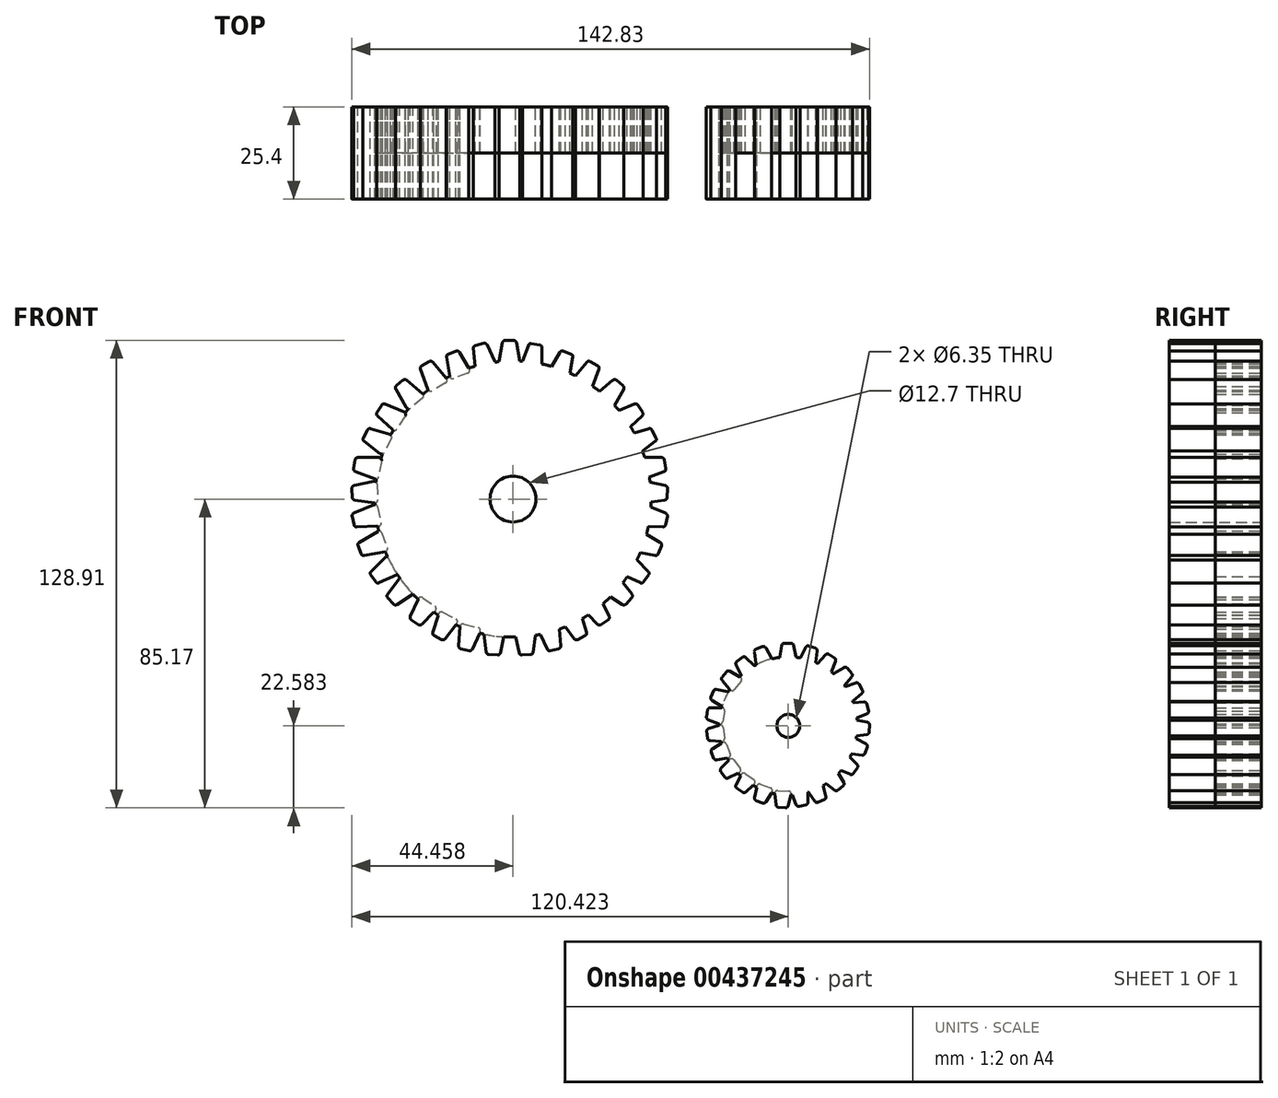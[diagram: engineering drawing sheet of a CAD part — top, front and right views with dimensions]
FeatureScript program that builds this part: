
annotation { "Feature Type Name" : "Feature", "Feature Type Description" : "" }
export const myFeature = defineFeature(function(context is Context, id is Id, definition is map)
    precondition{}
    {
        {
            var Q0;
            Q0=qCreatedBy(makeId("Front.planeOp"),FACE);
            var sketch = newSketch(context, id + "F0", { "sketchPlane" : qUnion([Q0])});
            skCircle(sketch, "E0", {"center": v(-38, 35.4) * mm, "radius": 38.1 * mm});
            skCircle(sketch, "E1", {"center": v(-38, 35.4) * mm, "radius": 6.35 * mm});
            skCircle(sketch, "E2", {"center": v(37.96, -27.19) * mm, "radius": 19.05 * mm});
            skCircle(sketch, "E3", {"center": v(37.96, -27.19) * mm, "radius": 3.18 * mm});
            skLineSegment(sketch, "E4", {"start": v(-32.93, 78.31) * mm, "end": v(-30.61, 77.9) * mm});
            skLineSegment(sketch, "E5", {"start": v(-33.78, 77.82) * mm, "end": v(-35.6, 72.8) * mm});
            skLineSegment(sketch, "E6", {"start": v(-29.98, 77.15) * mm, "end": v(-29.98, 71.81) * mm});
            skLineSegment(sketch, "E7", {"start": v(-35.02, 71.8) * mm, "end": v(-30.88, 71.06) * mm});
            skArc(sketch, "E8.filletArc", {"start": v(-32.93, 78.31) * mm, "mid": v(-33.45, 78.22) * mm, "end": v(-33.78, 77.82) * mm});
            skArc(sketch, "E9.filletArc", {"start": v(-29.98, 77.15) * mm, "mid": v(-30.16, 77.64) * mm, "end": v(-30.61, 77.9) * mm});
            skArc(sketch, "E10.filletArc", {"start": v(-30.88, 71.06) * mm, "mid": v(-30.25, 71.23) * mm, "end": v(-29.98, 71.81) * mm});
            skArc(sketch, "E11.filletArc", {"start": v(-35.6, 72.8) * mm, "mid": v(-35.55, 72.16) * mm, "end": v(-35.02, 71.8) * mm});
            skLineSegment(sketch, "E12", {"start": v(-24.2, 76.17) * mm, "end": v(-21.98, 75.37) * mm});
            skLineSegment(sketch, "E13", {"start": v(-25.11, 75.84) * mm, "end": v(-27.78, 71.21) * mm});
            skLineSegment(sketch, "E14", {"start": v(-21.49, 74.52) * mm, "end": v(-22.41, 69.26) * mm});
            skLineSegment(sketch, "E15", {"start": v(-27.38, 70.12) * mm, "end": v(-23.43, 68.68) * mm});
            skArc(sketch, "E16.filletArc", {"start": v(-24.2, 76.17) * mm, "mid": v(-24.71, 76.17) * mm, "end": v(-25.11, 75.84) * mm});
            skArc(sketch, "E17.filletArc", {"start": v(-21.49, 74.52) * mm, "mid": v(-21.58, 75.03) * mm, "end": v(-21.98, 75.37) * mm});
            skArc(sketch, "E18.filletArc", {"start": v(-23.43, 68.68) * mm, "mid": v(-22.78, 68.73) * mm, "end": v(-22.41, 69.26) * mm});
            skArc(sketch, "E19.filletArc", {"start": v(-27.78, 71.21) * mm, "mid": v(-27.84, 70.57) * mm, "end": v(-27.38, 70.12) * mm});
            skLineSegment(sketch, "E20", {"start": v(-16.67, 73.32) * mm, "end": v(-14.63, 72.15) * mm});
            skLineSegment(sketch, "E21", {"start": v(-17.63, 73.15) * mm, "end": v(-21.46, 68.6) * mm});
            skLineSegment(sketch, "E22", {"start": v(-14.3, 71.23) * mm, "end": v(-16.33, 65.64) * mm});
            skLineSegment(sketch, "E23", {"start": v(-21.25, 67.45) * mm, "end": v(-17.42, 65.24) * mm});
            skArc(sketch, "E24.filletArc", {"start": v(-16.67, 73.32) * mm, "mid": v(-17.18, 73.42) * mm, "end": v(-17.63, 73.15) * mm});
            skArc(sketch, "E25.filletArc", {"start": v(-14.3, 71.23) * mm, "mid": v(-14.3, 71.75) * mm, "end": v(-14.63, 72.15) * mm});
            skArc(sketch, "E26.filletArc", {"start": v(-17.42, 65.24) * mm, "mid": v(-16.78, 65.18) * mm, "end": v(-16.33, 65.64) * mm});
            skArc(sketch, "E27.filletArc", {"start": v(-21.46, 68.6) * mm, "mid": v(-21.62, 67.98) * mm, "end": v(-21.25, 67.45) * mm});
            skLineSegment(sketch, "E28", {"start": v(-9.46, 68.17) * mm, "end": v(-7.65, 66.66) * mm});
            skLineSegment(sketch, "E29", {"start": v(-10.44, 68.17) * mm, "end": v(-14.87, 64.45) * mm});
            skLineSegment(sketch, "E30", {"start": v(-7.48, 65.7) * mm, "end": v(-10.38, 60.68) * mm});
            skLineSegment(sketch, "E31", {"start": v(-14.87, 63.28) * mm, "end": v(-11.53, 60.48) * mm});
            skArc(sketch, "E32.filletArc", {"start": v(-9.46, 68.17) * mm, "mid": v(-9.95, 68.35) * mm, "end": v(-10.44, 68.17) * mm});
            skArc(sketch, "E33.filletArc", {"start": v(-7.48, 65.7) * mm, "mid": v(-7.4, 66.2) * mm, "end": v(-7.65, 66.66) * mm});
            skArc(sketch, "E34.filletArc", {"start": v(-11.53, 60.48) * mm, "mid": v(-10.9, 60.3) * mm, "end": v(-10.38, 60.68) * mm});
            skArc(sketch, "E35.filletArc", {"start": v(-14.87, 64.45) * mm, "mid": v(-15.15, 63.87) * mm, "end": v(-14.87, 63.28) * mm});
            skLineSegment(sketch, "E36", {"start": v(-3.53, 61.31) * mm, "end": v(-2.26, 59.32) * mm});
            skLineSegment(sketch, "E37", {"start": v(-4.47, 61.6) * mm, "end": v(-9.74, 59.41) * mm});
            skLineSegment(sketch, "E38", {"start": v(-2.4, 58.35) * mm, "end": v(-6.6, 54.49) * mm});
            skLineSegment(sketch, "E39", {"start": v(-10.09, 58.3) * mm, "end": v(-7.75, 54.64) * mm});
            skArc(sketch, "E40.filletArc", {"start": v(-3.53, 61.31) * mm, "mid": v(-3.95, 61.63) * mm, "end": v(-4.47, 61.6) * mm});
            skArc(sketch, "E41.filletArc", {"start": v(-2.4, 58.35) * mm, "mid": v(-2.15, 58.81) * mm, "end": v(-2.26, 59.32) * mm});
            skArc(sketch, "E42.filletArc", {"start": v(-7.75, 54.64) * mm, "mid": v(-7.2, 54.3) * mm, "end": v(-6.6, 54.49) * mm});
            skArc(sketch, "E43.filletArc", {"start": v(-9.74, 59.41) * mm, "mid": v(-10.17, 58.94) * mm, "end": v(-10.09, 58.3) * mm});
            skLineSegment(sketch, "E44", {"start": v(0.36, 54.44) * mm, "end": v(1.48, 52.26) * mm});
            skLineSegment(sketch, "E45", {"start": v(-0.54, 54.82) * mm, "end": v(-5.83, 53.19) * mm});
            skLineSegment(sketch, "E46", {"start": v(1.26, 51.3) * mm, "end": v(-3.15, 47.96) * mm});
            skLineSegment(sketch, "E47", {"start": v(-6.29, 52.11) * mm, "end": v(-4.3, 48.22) * mm});
            skArc(sketch, "E48.filletArc", {"start": v(0.36, 54.44) * mm, "mid": v(-0.02, 54.8) * mm, "end": v(-0.54, 54.82) * mm});
            skArc(sketch, "E49.filletArc", {"start": v(1.26, 51.3) * mm, "mid": v(1.54, 51.75) * mm, "end": v(1.48, 52.26) * mm});
            skArc(sketch, "E50.filletArc", {"start": v(-4.3, 48.22) * mm, "mid": v(-3.78, 47.83) * mm, "end": v(-3.15, 47.96) * mm});
            skArc(sketch, "E51.filletArc", {"start": v(-5.83, 53.19) * mm, "mid": v(-6.31, 52.76) * mm, "end": v(-6.29, 52.11) * mm});
            skLineSegment(sketch, "E52", {"start": v(3.74, 46.22) * mm, "end": v(4.16, 43.8) * mm});
            skLineSegment(sketch, "E53", {"start": v(2.99, 46.85) * mm, "end": v(-2.8, 46.85) * mm});
            skLineSegment(sketch, "E54", {"start": v(3.67, 42.95) * mm, "end": v(-1.76, 40.97) * mm});
            skLineSegment(sketch, "E55", {"start": v(-3.54, 45.95) * mm, "end": v(-2.77, 41.56) * mm});
            skArc(sketch, "E56.filletArc", {"start": v(3.74, 46.22) * mm, "mid": v(3.48, 46.67) * mm, "end": v(2.99, 46.85) * mm});
            skArc(sketch, "E57.filletArc", {"start": v(3.67, 42.95) * mm, "mid": v(4.07, 43.29) * mm, "end": v(4.16, 43.8) * mm});
            skArc(sketch, "E58.filletArc", {"start": v(-2.77, 41.56) * mm, "mid": v(-2.4, 41.03) * mm, "end": v(-1.76, 40.97) * mm});
            skArc(sketch, "E59.filletArc", {"start": v(-2.8, 46.85) * mm, "mid": v(-3.38, 46.58) * mm, "end": v(-3.54, 45.95) * mm});
            skLineSegment(sketch, "E60", {"start": v(4.62, 38.32) * mm, "end": v(4.52, 35.84) * mm});
            skLineSegment(sketch, "E61", {"start": v(4.03, 39.1) * mm, "end": v(-1.4, 40.3) * mm});
            skLineSegment(sketch, "E62", {"start": v(3.86, 35.11) * mm, "end": v(-1.66, 34.38) * mm});
            skLineSegment(sketch, "E63", {"start": v(-2.33, 39.58) * mm, "end": v(-2.52, 35.17) * mm});
            skArc(sketch, "E64.filletArc", {"start": v(4.62, 38.32) * mm, "mid": v(4.47, 38.82) * mm, "end": v(4.03, 39.1) * mm});
            skArc(sketch, "E65.filletArc", {"start": v(3.86, 35.11) * mm, "mid": v(4.32, 35.36) * mm, "end": v(4.52, 35.84) * mm});
            skArc(sketch, "E66.filletArc", {"start": v(-2.52, 35.17) * mm, "mid": v(-2.27, 34.57) * mm, "end": v(-1.66, 34.38) * mm});
            skArc(sketch, "E67.filletArc", {"start": v(-1.4, 40.3) * mm, "mid": v(-2.04, 40.16) * mm, "end": v(-2.33, 39.58) * mm});
            skLineSegment(sketch, "E68", {"start": v(4.59, 30.6) * mm, "end": v(4.09, 28.3) * mm});
            skLineSegment(sketch, "E69", {"start": v(4.13, 31.47) * mm, "end": v(-1.47, 33.76) * mm});
            skLineSegment(sketch, "E70", {"start": v(3.31, 27.7) * mm, "end": v(-2.73, 27.93) * mm});
            skLineSegment(sketch, "E71", {"start": v(-2.5, 33.21) * mm, "end": v(-3.45, 28.85) * mm});
            skArc(sketch, "E72.filletArc", {"start": v(4.59, 30.6) * mm, "mid": v(4.52, 31.12) * mm, "end": v(4.13, 31.47) * mm});
            skArc(sketch, "E73.filletArc", {"start": v(3.31, 27.7) * mm, "mid": v(3.8, 27.86) * mm, "end": v(4.09, 28.3) * mm});
            skArc(sketch, "E74.filletArc", {"start": v(-3.45, 28.85) * mm, "mid": v(-3.3, 28.23) * mm, "end": v(-2.73, 27.93) * mm});
            skArc(sketch, "E75.filletArc", {"start": v(-1.47, 33.76) * mm, "mid": v(-2.11, 33.73) * mm, "end": v(-2.5, 33.21) * mm});
            skLineSegment(sketch, "E76", {"start": v(2.93, 22.54) * mm, "end": v(2.11, 20.33) * mm});
            skLineSegment(sketch, "E77", {"start": v(2.6, 23.46) * mm, "end": v(-2.53, 26.46) * mm});
            skLineSegment(sketch, "E78", {"start": v(1.26, 19.84) * mm, "end": v(-4.59, 20.9) * mm});
            skLineSegment(sketch, "E79", {"start": v(-3.63, 26.07) * mm, "end": v(-5.17, 21.92) * mm});
            skArc(sketch, "E80.filletArc", {"start": v(2.93, 22.54) * mm, "mid": v(2.93, 23.06) * mm, "end": v(2.6, 23.46) * mm});
            skArc(sketch, "E81.filletArc", {"start": v(1.26, 19.84) * mm, "mid": v(1.78, 19.93) * mm, "end": v(2.11, 20.33) * mm});
            skArc(sketch, "E82.filletArc", {"start": v(-5.17, 21.92) * mm, "mid": v(-5.11, 21.28) * mm, "end": v(-4.59, 20.9) * mm});
            skArc(sketch, "E83.filletArc", {"start": v(-2.53, 26.46) * mm, "mid": v(-3.17, 26.52) * mm, "end": v(-3.63, 26.07) * mm});
            skLineSegment(sketch, "E84", {"start": v(-0.6, 14.48) * mm, "end": v(-1.95, 12.55) * mm});
            skLineSegment(sketch, "E85", {"start": v(-0.68, 15.46) * mm, "end": v(-4.45, 19.23) * mm});
            skLineSegment(sketch, "E86", {"start": v(-2.9, 12.3) * mm, "end": v(-7.73, 14.55) * mm});
            skLineSegment(sketch, "E87", {"start": v(-5.62, 19.13) * mm, "end": v(-8.03, 15.68) * mm});
            skArc(sketch, "E88.filletArc", {"start": v(-0.6, 14.48) * mm, "mid": v(-0.46, 14.99) * mm, "end": v(-0.68, 15.46) * mm});
            skArc(sketch, "E89.filletArc", {"start": v(-2.9, 12.3) * mm, "mid": v(-2.37, 12.25) * mm, "end": v(-1.95, 12.55) * mm});
            skArc(sketch, "E90.filletArc", {"start": v(-8.03, 15.68) * mm, "mid": v(-8.14, 15.05) * mm, "end": v(-7.73, 14.55) * mm});
            skArc(sketch, "E91.filletArc", {"start": v(-4.45, 19.23) * mm, "mid": v(-5.06, 19.45) * mm, "end": v(-5.62, 19.13) * mm});
            skLineSegment(sketch, "E92", {"start": v(-5.26, 8.14) * mm, "end": v(-6.86, 6.41) * mm});
            skLineSegment(sketch, "E93", {"start": v(-5.2, 9.12) * mm, "end": v(-8.43, 13.37) * mm});
            skLineSegment(sketch, "E94", {"start": v(-7.83, 6.29) * mm, "end": v(-12.32, 9.18) * mm});
            skLineSegment(sketch, "E95", {"start": v(-9.6, 13.43) * mm, "end": v(-12.46, 10.34) * mm});
            skArc(sketch, "E96.filletArc", {"start": v(-5.26, 8.14) * mm, "mid": v(-5.05, 8.62) * mm, "end": v(-5.2, 9.12) * mm});
            skArc(sketch, "E97.filletArc", {"start": v(-7.83, 6.29) * mm, "mid": v(-7.32, 6.17) * mm, "end": v(-6.86, 6.41) * mm});
            skArc(sketch, "E98.filletArc", {"start": v(-12.46, 10.34) * mm, "mid": v(-12.66, 9.73) * mm, "end": v(-12.32, 9.18) * mm});
            skArc(sketch, "E99.filletArc", {"start": v(-8.43, 13.37) * mm, "mid": v(-9, 13.67) * mm, "end": v(-9.6, 13.43) * mm});
            skLineSegment(sketch, "E100", {"start": v(-11.74, 2.11) * mm, "end": v(-13.67, 0.76) * mm});
            skLineSegment(sketch, "E101", {"start": v(-11.49, 3.06) * mm, "end": v(-13.75, 7.9) * mm});
            skLineSegment(sketch, "E102", {"start": v(-14.65, 0.84) * mm, "end": v(-18.43, 4.62) * mm});
            skLineSegment(sketch, "E103", {"start": v(-14.87, 8.2) * mm, "end": v(-18.32, 5.78) * mm});
            skArc(sketch, "E104.filletArc", {"start": v(-11.74, 2.11) * mm, "mid": v(-11.44, 2.54) * mm, "end": v(-11.49, 3.06) * mm});
            skArc(sketch, "E105.filletArc", {"start": v(-14.65, 0.84) * mm, "mid": v(-14.18, 0.62) * mm, "end": v(-13.67, 0.76) * mm});
            skArc(sketch, "E106.filletArc", {"start": v(-18.32, 5.78) * mm, "mid": v(-18.65, 5.23) * mm, "end": v(-18.43, 4.62) * mm});
            skArc(sketch, "E107.filletArc", {"start": v(-13.75, 7.9) * mm, "mid": v(-14.24, 8.31) * mm, "end": v(-14.87, 8.2) * mm});
            skLineSegment(sketch, "E108", {"start": v(-18.08, -2.27) * mm, "end": v(-20.17, -3.35) * mm});
            skLineSegment(sketch, "E109", {"start": v(-17.7, -1.37) * mm, "end": v(-19.27, 3.73) * mm});
            skLineSegment(sketch, "E110", {"start": v(-21.13, -3.13) * mm, "end": v(-24.36, 1.12) * mm});
            skLineSegment(sketch, "E111", {"start": v(-20.35, 4.18) * mm, "end": v(-24.1, 2.26) * mm});
            skArc(sketch, "E112.filletArc", {"start": v(-18.08, -2.27) * mm, "mid": v(-17.72, -1.89) * mm, "end": v(-17.7, -1.37) * mm});
            skArc(sketch, "E113.filletArc", {"start": v(-21.13, -3.13) * mm, "mid": v(-20.7, -3.41) * mm, "end": v(-20.17, -3.35) * mm});
            skArc(sketch, "E114.filletArc", {"start": v(-24.1, 2.26) * mm, "mid": v(-24.5, 1.75) * mm, "end": v(-24.36, 1.12) * mm});
            skArc(sketch, "E115.filletArc", {"start": v(-19.27, 3.73) * mm, "mid": v(-19.7, 4.2) * mm, "end": v(-20.35, 4.18) * mm});
            skLineSegment(sketch, "E116", {"start": v(-25.4, -5.88) * mm, "end": v(-27.7, -6.46) * mm});
            skLineSegment(sketch, "E117", {"start": v(-24.83, -5.08) * mm, "end": v(-25.24, 0.24) * mm});
            skLineSegment(sketch, "E118", {"start": v(-28.57, -6.03) * mm, "end": v(-30.77, -1.17) * mm});
            skLineSegment(sketch, "E119", {"start": v(-26.18, 0.93) * mm, "end": v(-30.27, -0.12) * mm});
            skArc(sketch, "E120.filletArc", {"start": v(-25.4, -5.88) * mm, "mid": v(-24.98, -5.58) * mm, "end": v(-24.83, -5.08) * mm});
            skArc(sketch, "E121.filletArc", {"start": v(-28.57, -6.03) * mm, "mid": v(-28.2, -6.4) * mm, "end": v(-27.7, -6.46) * mm});
            skArc(sketch, "E122.filletArc", {"start": v(-30.27, -0.12) * mm, "mid": v(-30.76, -0.52) * mm, "end": v(-30.77, -1.17) * mm});
            skArc(sketch, "E123.filletArc", {"start": v(-25.24, 0.24) * mm, "mid": v(-25.55, 0.8) * mm, "end": v(-26.18, 0.93) * mm});
            skLineSegment(sketch, "E124", {"start": v(-33.2, -7.52) * mm, "end": v(-35.55, -7.63) * mm});
            skLineSegment(sketch, "E125", {"start": v(-32.47, -6.86) * mm, "end": v(-31.78, -1.57) * mm});
            skLineSegment(sketch, "E126", {"start": v(-36.32, -7.03) * mm, "end": v(-37.48, -1.82) * mm});
            skLineSegment(sketch, "E127", {"start": v(-32.56, -0.7) * mm, "end": v(-36.77, -0.9) * mm});
            skArc(sketch, "E128.filletArc", {"start": v(-33.2, -7.52) * mm, "mid": v(-32.7, -7.32) * mm, "end": v(-32.47, -6.86) * mm});
            skArc(sketch, "E129.filletArc", {"start": v(-36.32, -7.03) * mm, "mid": v(-36.04, -7.47) * mm, "end": v(-35.55, -7.63) * mm});
            skArc(sketch, "E130.filletArc", {"start": v(-36.77, -0.9) * mm, "mid": v(-37.34, -1.2) * mm, "end": v(-37.48, -1.82) * mm});
            skArc(sketch, "E131.filletArc", {"start": v(-31.78, -1.57) * mm, "mid": v(-31.97, -0.95) * mm, "end": v(-32.56, -0.7) * mm});
            skArc(sketch, "E132.MirrorCS", {"start": v(-59.5, 5.78) * mm, "mid": v(-59.18, 5.23) * mm, "end": v(-59.4, 4.62) * mm});
            skArc(sketch, "E133.MirrorCS", {"start": v(-74.39, 28.85) * mm, "mid": v(-74.53, 28.23) * mm, "end": v(-75.1, 27.93) * mm});
            skArc(sketch, "E134.MirrorCS", {"start": v(-63.18, 0.84) * mm, "mid": v(-63.65, 0.62) * mm, "end": v(-64.16, 0.76) * mm});
            skArc(sketch, "E135.MirrorCS", {"start": v(-81.5, 42.95) * mm, "mid": v(-81.9, 43.29) * mm, "end": v(-82, 43.8) * mm});
            skArc(sketch, "E136.MirrorCS", {"start": v(-74.3, 61.31) * mm, "mid": v(-73.88, 61.63) * mm, "end": v(-73.36, 61.6) * mm});
            skArc(sketch, "E137.MirrorCS", {"start": v(-81.57, 46.22) * mm, "mid": v(-81.3, 46.67) * mm, "end": v(-80.82, 46.85) * mm});
            skArc(sketch, "E138.MirrorCS", {"start": v(-82.42, 30.6) * mm, "mid": v(-82.35, 31.12) * mm, "end": v(-81.96, 31.47) * mm});
            skLineSegment(sketch, "E139.MirrorCS", {"start": v(-82.42, 30.6) * mm, "end": v(-81.92, 28.3) * mm});
            skLineSegment(sketch, "E140.MirrorCS", {"start": v(-66.09, 2.11) * mm, "end": v(-64.16, 0.76) * mm});
            skLineSegment(sketch, "E141.MirrorCS", {"start": v(-74.3, 61.31) * mm, "end": v(-75.57, 59.32) * mm});
            skLineSegment(sketch, "E142.MirrorCS", {"start": v(-81.57, 46.22) * mm, "end": v(-82, 43.8) * mm});
            skArc(sketch, "E143.MirrorCS", {"start": v(-44.64, -7.52) * mm, "mid": v(-45.12, -7.32) * mm, "end": v(-45.36, -6.86) * mm});
            skArc(sketch, "E144.MirrorCS", {"start": v(-68.37, 68.17) * mm, "mid": v(-67.88, 68.35) * mm, "end": v(-67.4, 68.17) * mm});
            skArc(sketch, "E145.MirrorCS", {"start": v(-59.75, -2.27) * mm, "mid": v(-60.1, -1.89) * mm, "end": v(-60.13, -1.37) * mm});
            skArc(sketch, "E146.MirrorCS", {"start": v(-75.3, 26.46) * mm, "mid": v(-74.66, 26.52) * mm, "end": v(-74.2, 26.07) * mm});
            skArc(sketch, "E147.MirrorCS", {"start": v(-58.56, 3.73) * mm, "mid": v(-58.12, 4.2) * mm, "end": v(-57.48, 4.18) * mm});
            skArc(sketch, "E148.MirrorCS", {"start": v(-50.05, 71.21) * mm, "mid": v(-50, 70.57) * mm, "end": v(-50.45, 70.12) * mm});
            skArc(sketch, "E149.MirrorCS", {"start": v(-56.37, 68.6) * mm, "mid": v(-56.2, 67.98) * mm, "end": v(-56.58, 67.45) * mm});
            skArc(sketch, "E150.MirrorCS", {"start": v(-54.4, 68.68) * mm, "mid": v(-55.05, 68.73) * mm, "end": v(-55.42, 69.26) * mm});
            skArc(sketch, "E151.MirrorCS", {"start": v(-72.67, 21.92) * mm, "mid": v(-72.72, 21.28) * mm, "end": v(-73.24, 20.9) * mm});
            skArc(sketch, "E152.MirrorCS", {"start": v(-73.38, 19.23) * mm, "mid": v(-72.77, 19.45) * mm, "end": v(-72.22, 19.13) * mm});
            skArc(sketch, "E153.MirrorCS", {"start": v(-52.6, 0.24) * mm, "mid": v(-52.28, 0.8) * mm, "end": v(-51.65, 0.93) * mm});
            skLineSegment(sketch, "E154.MirrorCS", {"start": v(-59.75, -2.27) * mm, "end": v(-57.66, -3.35) * mm});
            skArc(sketch, "E155.MirrorCS", {"start": v(-53.73, 2.26) * mm, "mid": v(-53.34, 1.75) * mm, "end": v(-53.47, 1.12) * mm});
            skLineSegment(sketch, "E156.MirrorCS", {"start": v(-68.37, 68.17) * mm, "end": v(-70.18, 66.66) * mm});
            skLineSegment(sketch, "E157.MirrorCS", {"start": v(-44.64, -7.52) * mm, "end": v(-42.28, -7.63) * mm});
            skArc(sketch, "E158.MirrorCS", {"start": v(-69.8, 15.68) * mm, "mid": v(-69.69, 15.05) * mm, "end": v(-70.1, 14.55) * mm});
            skArc(sketch, "E159.MirrorCS", {"start": v(-47.57, -0.12) * mm, "mid": v(-47.07, -0.52) * mm, "end": v(-47.06, -1.17) * mm});
            skArc(sketch, "E160.MirrorCS", {"start": v(-60.4, 65.24) * mm, "mid": v(-61.05, 65.18) * mm, "end": v(-61.5, 65.64) * mm});
            skArc(sketch, "E161.MirrorCS", {"start": v(-70.08, 54.64) * mm, "mid": v(-70.62, 54.3) * mm, "end": v(-71.24, 54.49) * mm});
            skArc(sketch, "E162.MirrorCS", {"start": v(-75.06, 41.56) * mm, "mid": v(-75.43, 41.03) * mm, "end": v(-76.07, 40.97) * mm});
            skArc(sketch, "E163.MirrorCS", {"start": v(-74.94, 12.3) * mm, "mid": v(-75.46, 12.25) * mm, "end": v(-75.89, 12.55) * mm});
            skArc(sketch, "E164.MirrorCS", {"start": v(-49.26, -6.03) * mm, "mid": v(-49.62, -6.4) * mm, "end": v(-50.14, -6.46) * mm});
            skArc(sketch, "E165.MirrorCS", {"start": v(-63.54, 71.23) * mm, "mid": v(-63.54, 71.75) * mm, "end": v(-63.2, 72.15) * mm});
            skArc(sketch, "E166.MirrorCS", {"start": v(-75.44, 58.35) * mm, "mid": v(-75.68, 58.81) * mm, "end": v(-75.57, 59.32) * mm});
            skArc(sketch, "E167.MirrorCS", {"start": v(-81.14, 27.7) * mm, "mid": v(-81.64, 27.86) * mm, "end": v(-81.92, 28.3) * mm});
            skArc(sketch, "E168.MirrorCS", {"start": v(-61.16, 73.32) * mm, "mid": v(-60.65, 73.42) * mm, "end": v(-60.2, 73.15) * mm});
            skArc(sketch, "E169.MirrorCS", {"start": v(-52.43, -5.88) * mm, "mid": v(-52.86, -5.58) * mm, "end": v(-53, -5.08) * mm});
            skLineSegment(sketch, "E170.MirrorCS", {"start": v(-72.22, 19.13) * mm, "end": v(-69.8, 15.68) * mm});
            skLineSegment(sketch, "E171.MirrorCS", {"start": v(-62.96, 8.2) * mm, "end": v(-59.5, 5.78) * mm});
            skLineSegment(sketch, "E172.MirrorCS", {"start": v(-51.65, 0.93) * mm, "end": v(-47.57, -0.12) * mm});
            skLineSegment(sketch, "E173.MirrorCS", {"start": v(-56.58, 67.45) * mm, "end": v(-60.4, 65.24) * mm});
            skLineSegment(sketch, "E174.MirrorCS", {"start": v(-67.74, 58.3) * mm, "end": v(-70.08, 54.64) * mm});
            skLineSegment(sketch, "E175.MirrorCS", {"start": v(-74.29, 45.95) * mm, "end": v(-75.06, 41.56) * mm});
            skLineSegment(sketch, "E176.MirrorCS", {"start": v(-75.33, 33.21) * mm, "end": v(-74.39, 28.85) * mm});
            skLineSegment(sketch, "E177.MirrorCS", {"start": v(-63.18, 0.84) * mm, "end": v(-59.4, 4.62) * mm});
            skLineSegment(sketch, "E178.MirrorCS", {"start": v(-63.54, 71.23) * mm, "end": v(-61.5, 65.64) * mm});
            skLineSegment(sketch, "E179.MirrorCS", {"start": v(-75.44, 58.35) * mm, "end": v(-71.24, 54.49) * mm});
            skLineSegment(sketch, "E180.MirrorCS", {"start": v(-81.5, 42.95) * mm, "end": v(-76.07, 40.97) * mm});
            skLineSegment(sketch, "E181.MirrorCS", {"start": v(-77.24, 14.48) * mm, "end": v(-75.89, 12.55) * mm});
            skLineSegment(sketch, "E182.MirrorCS", {"start": v(-52.43, -5.88) * mm, "end": v(-50.14, -6.46) * mm});
            skLineSegment(sketch, "E183.MirrorCS", {"start": v(-61.16, 73.32) * mm, "end": v(-63.2, 72.15) * mm});
            skLineSegment(sketch, "E184.MirrorCS", {"start": v(-77.15, 15.46) * mm, "end": v(-73.38, 19.23) * mm});
            skLineSegment(sketch, "E185.MirrorCS", {"start": v(-66.34, 3.06) * mm, "end": v(-64.09, 7.9) * mm});
            skLineSegment(sketch, "E186.MirrorCS", {"start": v(-60.2, 73.15) * mm, "end": v(-56.37, 68.6) * mm});
            skArc(sketch, "E187.MirrorCS", {"start": v(-82.45, 38.32) * mm, "mid": v(-82.3, 38.82) * mm, "end": v(-81.86, 39.1) * mm});
            skArc(sketch, "E188.MirrorCS", {"start": v(-80.76, 22.54) * mm, "mid": v(-80.77, 23.06) * mm, "end": v(-80.43, 23.46) * mm});
            skArc(sketch, "E189.MirrorCS", {"start": v(-72.57, 8.14) * mm, "mid": v(-72.78, 8.62) * mm, "end": v(-72.62, 9.12) * mm});
            skArc(sketch, "E190.MirrorCS", {"start": v(-78.2, 54.44) * mm, "mid": v(-77.8, 54.8) * mm, "end": v(-77.29, 54.82) * mm});
            skLineSegment(sketch, "E191.MirrorCS", {"start": v(-81.96, 31.47) * mm, "end": v(-76.36, 33.76) * mm});
            skLineSegment(sketch, "E192.MirrorCS", {"start": v(-45.27, -0.7) * mm, "end": v(-41.06, -0.9) * mm});
            skArc(sketch, "E193.MirrorCS", {"start": v(-46.06, -1.57) * mm, "mid": v(-45.86, -0.95) * mm, "end": v(-45.27, -0.7) * mm});
            skArc(sketch, "E194.MirrorCS", {"start": v(-76.42, 40.3) * mm, "mid": v(-75.8, 40.16) * mm, "end": v(-75.5, 39.58) * mm});
            skArc(sketch, "E195.MirrorCS", {"start": v(-69.4, 13.37) * mm, "mid": v(-68.83, 13.67) * mm, "end": v(-68.23, 13.43) * mm});
            skArc(sketch, "E196.MirrorCS", {"start": v(-62.96, 64.45) * mm, "mid": v(-62.69, 63.87) * mm, "end": v(-62.96, 63.28) * mm});
            skLineSegment(sketch, "E197.MirrorCS", {"start": v(-75.5, 39.58) * mm, "end": v(-75.31, 35.17) * mm});
            skArc(sketch, "E198.MirrorCS", {"start": v(-72, 53.19) * mm, "mid": v(-71.52, 52.76) * mm, "end": v(-71.54, 52.11) * mm});
            skLineSegment(sketch, "E199.MirrorCS", {"start": v(-74.2, 26.07) * mm, "end": v(-72.67, 21.92) * mm});
            skLineSegment(sketch, "E200.MirrorCS", {"start": v(-68.23, 13.43) * mm, "end": v(-65.37, 10.34) * mm});
            skLineSegment(sketch, "E201.MirrorCS", {"start": v(-57.48, 4.18) * mm, "end": v(-53.73, 2.26) * mm});
            skLineSegment(sketch, "E202.MirrorCS", {"start": v(-62.96, 63.28) * mm, "end": v(-66.3, 60.48) * mm});
            skLineSegment(sketch, "E203.MirrorCS", {"start": v(-50.45, 70.12) * mm, "end": v(-54.4, 68.68) * mm});
            skLineSegment(sketch, "E204.MirrorCS", {"start": v(-71.54, 52.11) * mm, "end": v(-73.54, 48.22) * mm});
            skLineSegment(sketch, "E205.MirrorCS", {"start": v(-70, 6.29) * mm, "end": v(-65.51, 9.18) * mm});
            skLineSegment(sketch, "E206.MirrorCS", {"start": v(-56.7, -3.13) * mm, "end": v(-53.47, 1.12) * mm});
            skLineSegment(sketch, "E207.MirrorCS", {"start": v(-81.69, 35.11) * mm, "end": v(-76.17, 34.38) * mm});
            skLineSegment(sketch, "E208.MirrorCS", {"start": v(-70.35, 65.7) * mm, "end": v(-67.45, 60.68) * mm});
            skLineSegment(sketch, "E209.MirrorCS", {"start": v(-67.4, 68.17) * mm, "end": v(-62.96, 64.45) * mm});
            skLineSegment(sketch, "E210.MirrorCS", {"start": v(-80.43, 23.46) * mm, "end": v(-75.3, 26.46) * mm});
            skArc(sketch, "E211.MirrorCS", {"start": v(-73.54, 48.22) * mm, "mid": v(-74.05, 47.83) * mm, "end": v(-74.68, 47.96) * mm});
            skArc(sketch, "E212.MirrorCS", {"start": v(-75.04, 46.85) * mm, "mid": v(-74.45, 46.58) * mm, "end": v(-74.29, 45.95) * mm});
            skArc(sketch, "E213.MirrorCS", {"start": v(-79.09, 51.3) * mm, "mid": v(-79.37, 51.75) * mm, "end": v(-79.3, 52.26) * mm});
            skLineSegment(sketch, "E214.MirrorCS", {"start": v(-82.45, 38.32) * mm, "end": v(-82.35, 35.84) * mm});
            skArc(sketch, "E215.MirrorCS", {"start": v(-76.36, 33.76) * mm, "mid": v(-75.72, 33.73) * mm, "end": v(-75.33, 33.21) * mm});
            skArc(sketch, "E216.MirrorCS", {"start": v(-68.1, 59.41) * mm, "mid": v(-67.66, 58.94) * mm, "end": v(-67.74, 58.3) * mm});
            skArc(sketch, "E217.MirrorCS", {"start": v(-70, 6.29) * mm, "mid": v(-70.5, 6.17) * mm, "end": v(-70.97, 6.41) * mm});
            skLineSegment(sketch, "E218.MirrorCS", {"start": v(-80.76, 22.54) * mm, "end": v(-79.94, 20.33) * mm});
            skLineSegment(sketch, "E219.MirrorCS", {"start": v(-78.2, 54.44) * mm, "end": v(-79.3, 52.26) * mm});
            skArc(sketch, "E220.MirrorCS", {"start": v(-70.35, 65.7) * mm, "mid": v(-70.44, 66.2) * mm, "end": v(-70.18, 66.66) * mm});
            skArc(sketch, "E221.MirrorCS", {"start": v(-66.3, 60.48) * mm, "mid": v(-66.93, 60.3) * mm, "end": v(-67.45, 60.68) * mm});
            skArc(sketch, "E222.MirrorCS", {"start": v(-75.31, 35.17) * mm, "mid": v(-75.56, 34.57) * mm, "end": v(-76.17, 34.38) * mm});
            skArc(sketch, "E223.MirrorCS", {"start": v(-81.69, 35.11) * mm, "mid": v(-82.15, 35.36) * mm, "end": v(-82.35, 35.84) * mm});
            skArc(sketch, "E224.MirrorCS", {"start": v(-79.1, 19.84) * mm, "mid": v(-79.6, 19.93) * mm, "end": v(-79.94, 20.33) * mm});
            skLineSegment(sketch, "E225.MirrorCS", {"start": v(-53.64, 76.17) * mm, "end": v(-55.85, 75.37) * mm});
            skArc(sketch, "E226.MirrorCS", {"start": v(-56.7, -3.13) * mm, "mid": v(-57.14, -3.41) * mm, "end": v(-57.66, -3.35) * mm});
            skArc(sketch, "E227.MirrorCS", {"start": v(-66.09, 2.11) * mm, "mid": v(-66.39, 2.54) * mm, "end": v(-66.34, 3.06) * mm});
            skArc(sketch, "E228.MirrorCS", {"start": v(-77.24, 14.48) * mm, "mid": v(-77.37, 14.99) * mm, "end": v(-77.15, 15.46) * mm});
            skLineSegment(sketch, "E229.MirrorCS", {"start": v(-72.57, 8.14) * mm, "end": v(-70.97, 6.41) * mm});
            skArc(sketch, "E230.MirrorCS", {"start": v(-64.09, 7.9) * mm, "mid": v(-63.6, 8.31) * mm, "end": v(-62.96, 8.2) * mm});
            skArc(sketch, "E231.MirrorCS", {"start": v(-56.34, 74.52) * mm, "mid": v(-56.25, 75.03) * mm, "end": v(-55.85, 75.37) * mm});
            skArc(sketch, "E232.MirrorCS", {"start": v(-41.5, -7.03) * mm, "mid": v(-41.79, -7.47) * mm, "end": v(-42.28, -7.63) * mm});
            skArc(sketch, "E233.MirrorCS", {"start": v(-65.37, 10.34) * mm, "mid": v(-65.17, 9.73) * mm, "end": v(-65.51, 9.18) * mm});
            skArc(sketch, "E234.MirrorCS", {"start": v(-41.06, -0.9) * mm, "mid": v(-40.49, -1.2) * mm, "end": v(-40.35, -1.82) * mm});
            skLineSegment(sketch, "E235.MirrorCS", {"start": v(-74.94, 12.3) * mm, "end": v(-70.1, 14.55) * mm});
            skLineSegment(sketch, "E236.MirrorCS", {"start": v(-49.26, -6.03) * mm, "end": v(-47.06, -1.17) * mm});
            skLineSegment(sketch, "E237.MirrorCS", {"start": v(-79.09, 51.3) * mm, "end": v(-74.68, 47.96) * mm});
            skLineSegment(sketch, "E238.MirrorCS", {"start": v(-72.62, 9.12) * mm, "end": v(-69.4, 13.37) * mm});
            skLineSegment(sketch, "E239.MirrorCS", {"start": v(-60.13, -1.37) * mm, "end": v(-58.56, 3.73) * mm});
            skLineSegment(sketch, "E240.MirrorCS", {"start": v(-77.29, 54.82) * mm, "end": v(-72, 53.19) * mm});
            skLineSegment(sketch, "E241.MirrorCS", {"start": v(-81.86, 39.1) * mm, "end": v(-76.42, 40.3) * mm});
            skLineSegment(sketch, "E242.MirrorCS", {"start": v(-81.14, 27.7) * mm, "end": v(-75.1, 27.93) * mm});
            skLineSegment(sketch, "E243.MirrorCS", {"start": v(-53, -5.08) * mm, "end": v(-52.6, 0.24) * mm});
            skLineSegment(sketch, "E244.MirrorCS", {"start": v(-73.36, 61.6) * mm, "end": v(-68.1, 59.41) * mm});
            skLineSegment(sketch, "E245.MirrorCS", {"start": v(-80.82, 46.85) * mm, "end": v(-75.04, 46.85) * mm});
            skLineSegment(sketch, "E246.MirrorCS", {"start": v(-41.5, -7.03) * mm, "end": v(-40.35, -1.82) * mm});
            skLineSegment(sketch, "E247.MirrorCS", {"start": v(-56.34, 74.52) * mm, "end": v(-55.42, 69.26) * mm});
            skLineSegment(sketch, "E248.MirrorCS", {"start": v(-79.1, 19.84) * mm, "end": v(-73.24, 20.9) * mm});
            skLineSegment(sketch, "E249.MirrorCS", {"start": v(-52.72, 75.84) * mm, "end": v(-50.05, 71.21) * mm});
            skLineSegment(sketch, "E250.MirrorCS", {"start": v(-45.36, -6.86) * mm, "end": v(-46.06, -1.57) * mm});
            skArc(sketch, "E251.MirrorCS", {"start": v(-53.64, 76.17) * mm, "mid": v(-53.12, 76.17) * mm, "end": v(-52.72, 75.84) * mm});
            skLineSegment(sketch, "E252", {"start": v(-40.17, 79.14) * mm, "end": v(-37.81, 79.14) * mm});
            skLineSegment(sketch, "E253", {"start": v(-40.92, 78.51) * mm, "end": v(-41.82, 73.43) * mm});
            skLineSegment(sketch, "E254", {"start": v(-37.06, 78.51) * mm, "end": v(-36.17, 73.43) * mm});
            skLineSegment(sketch, "E255", {"start": v(-41.07, 72.53) * mm, "end": v(-36.92, 72.53) * mm});
            skArc(sketch, "E256.filletArc", {"start": v(-40.17, 79.14) * mm, "mid": v(-40.66, 78.96) * mm, "end": v(-40.92, 78.51) * mm});
            skArc(sketch, "E257.filletArc", {"start": v(-37.06, 78.51) * mm, "mid": v(-37.32, 78.96) * mm, "end": v(-37.81, 79.14) * mm});
            skArc(sketch, "E258.filletArc", {"start": v(-36.92, 72.53) * mm, "mid": v(-36.33, 72.8) * mm, "end": v(-36.17, 73.43) * mm});
            skArc(sketch, "E259.filletArc", {"start": v(-41.82, 73.43) * mm, "mid": v(-41.65, 72.8) * mm, "end": v(-41.07, 72.53) * mm});
            skLineSegment(sketch, "E260", {"start": v(-48.37, 77.75) * mm, "end": v(-46.1, 78.36) * mm});
            skLineSegment(sketch, "E261", {"start": v(-48.93, 76.95) * mm, "end": v(-48.48, 71.8) * mm});
            skLineSegment(sketch, "E262", {"start": v(-45.2, 77.95) * mm, "end": v(-43.02, 73.27) * mm});
            skLineSegment(sketch, "E263", {"start": v(-47.53, 71.14) * mm, "end": v(-43.52, 72.21) * mm});
            skArc(sketch, "E264.filletArc", {"start": v(-48.37, 77.75) * mm, "mid": v(-48.8, 77.45) * mm, "end": v(-48.93, 76.95) * mm});
            skArc(sketch, "E265.filletArc", {"start": v(-45.2, 77.95) * mm, "mid": v(-45.57, 78.32) * mm, "end": v(-46.1, 78.36) * mm});
            skArc(sketch, "E266.filletArc", {"start": v(-43.52, 72.21) * mm, "mid": v(-43.02, 72.63) * mm, "end": v(-43.02, 73.27) * mm});
            skArc(sketch, "E267.filletArc", {"start": v(-48.48, 71.8) * mm, "mid": v(-48.16, 71.25) * mm, "end": v(-47.53, 71.14) * mm});
            skLineSegment(sketch, "E268", {"start": v(43.64, -5.13) * mm, "end": v(45.42, -5.7) * mm});
            skLineSegment(sketch, "E269", {"start": v(45.94, -6.52) * mm, "end": v(45.55, -9.68) * mm});
            skLineSegment(sketch, "E270", {"start": v(42.73, -5.51) * mm, "end": v(41.3, -8.33) * mm});
            skArc(sketch, "E271.filletArc", {"start": v(43.64, -5.13) * mm, "mid": v(43.11, -5.15) * mm, "end": v(42.73, -5.51) * mm});
            skArc(sketch, "E272.filletArc", {"start": v(45.94, -6.52) * mm, "mid": v(45.83, -6.01) * mm, "end": v(45.42, -5.7) * mm});
            skArc(sketch, "E273.filletArc", {"start": v(41.3, -8.33) * mm, "mid": v(41.27, -8.97) * mm, "end": v(41.75, -9.4) * mm});
            skLineSegment(sketch, "E274", {"start": v(41.75, -9.4) * mm, "end": v(44.56, -10.31) * mm});
            skArc(sketch, "E275.filletArc", {"start": v(44.56, -10.31) * mm, "mid": v(45.2, -10.23) * mm, "end": v(45.55, -9.68) * mm});
            skLineSegment(sketch, "E276", {"start": v(49.17, -7.45) * mm, "end": v(50.7, -8.42) * mm});
            skLineSegment(sketch, "E277", {"start": v(51, -9.34) * mm, "end": v(49.76, -12.46) * mm});
            skLineSegment(sketch, "E278", {"start": v(48.2, -7.59) * mm, "end": v(45.98, -10.07) * mm});
            skArc(sketch, "E279.filletArc", {"start": v(49.17, -7.45) * mm, "mid": v(48.65, -7.34) * mm, "end": v(48.2, -7.59) * mm});
            skArc(sketch, "E280.filletArc", {"start": v(51, -9.34) * mm, "mid": v(51.01, -8.83) * mm, "end": v(50.7, -8.42) * mm});
            skArc(sketch, "E281.filletArc", {"start": v(45.98, -10.07) * mm, "mid": v(45.8, -10.7) * mm, "end": v(46.14, -11.23) * mm});
            skLineSegment(sketch, "E282", {"start": v(46.14, -11.23) * mm, "end": v(48.64, -12.82) * mm});
            skArc(sketch, "E283.filletArc", {"start": v(48.64, -12.82) * mm, "mid": v(49.28, -12.9) * mm, "end": v(49.76, -12.46) * mm});
            skLineSegment(sketch, "E284", {"start": v(54.25, -11.25) * mm, "end": v(55.45, -12.68) * mm});
            skLineSegment(sketch, "E285", {"start": v(55.46, -13.66) * mm, "end": v(53.44, -16.12) * mm});
            skLineSegment(sketch, "E286", {"start": v(53.28, -11.09) * mm, "end": v(50.56, -12.7) * mm});
            skArc(sketch, "E287.filletArc", {"start": v(54.25, -11.25) * mm, "mid": v(53.8, -11) * mm, "end": v(53.28, -11.09) * mm});
            skArc(sketch, "E288.filletArc", {"start": v(55.46, -13.66) * mm, "mid": v(55.63, -13.17) * mm, "end": v(55.45, -12.68) * mm});
            skArc(sketch, "E289.filletArc", {"start": v(50.56, -12.7) * mm, "mid": v(50.2, -13.23) * mm, "end": v(50.37, -13.85) * mm});
            skLineSegment(sketch, "E290", {"start": v(50.37, -13.85) * mm, "end": v(52.26, -16.13) * mm});
            skArc(sketch, "E291.filletArc", {"start": v(52.26, -16.13) * mm, "mid": v(52.85, -16.4) * mm, "end": v(53.44, -16.12) * mm});
            skLineSegment(sketch, "E292", {"start": v(57.46, -15.65) * mm, "end": v(58.4, -17.27) * mm});
            skLineSegment(sketch, "E293", {"start": v(58.24, -18.23) * mm, "end": v(55.82, -20.3) * mm});
            skLineSegment(sketch, "E294", {"start": v(56.54, -15.32) * mm, "end": v(53.58, -16.44) * mm});
            skArc(sketch, "E295.filletArc", {"start": v(57.46, -15.65) * mm, "mid": v(57.06, -15.31) * mm, "end": v(56.54, -15.32) * mm});
            skArc(sketch, "E296.filletArc", {"start": v(58.24, -18.23) * mm, "mid": v(58.49, -17.78) * mm, "end": v(58.4, -17.27) * mm});
            skArc(sketch, "E297.filletArc", {"start": v(53.58, -16.44) * mm, "mid": v(53.12, -16.9) * mm, "end": v(53.19, -17.54) * mm});
            skLineSegment(sketch, "E298", {"start": v(53.19, -17.54) * mm, "end": v(54.66, -20.1) * mm});
            skArc(sketch, "E299.filletArc", {"start": v(54.66, -20.1) * mm, "mid": v(55.2, -20.48) * mm, "end": v(55.82, -20.3) * mm});
            skLineSegment(sketch, "E300", {"start": v(59.69, -21.2) * mm, "end": v(60.08, -23.02) * mm});
            skLineSegment(sketch, "E301", {"start": v(59.64, -23.88) * mm, "end": v(56.7, -25.12) * mm});
            skLineSegment(sketch, "E302", {"start": v(58.9, -20.6) * mm, "end": v(55.74, -20.76) * mm});
            skArc(sketch, "E303.filletArc", {"start": v(59.69, -21.2) * mm, "mid": v(59.4, -20.75) * mm, "end": v(58.9, -20.6) * mm});
            skArc(sketch, "E304.filletArc", {"start": v(59.64, -23.88) * mm, "mid": v(60.02, -23.53) * mm, "end": v(60.08, -23.02) * mm});
            skArc(sketch, "E305.filletArc", {"start": v(55.74, -20.76) * mm, "mid": v(55.17, -21.06) * mm, "end": v(55.04, -21.69) * mm});
            skLineSegment(sketch, "E306", {"start": v(55.04, -21.69) * mm, "end": v(55.66, -24.58) * mm});
            skArc(sketch, "E307.filletArc", {"start": v(55.66, -24.58) * mm, "mid": v(56.05, -25.1) * mm, "end": v(56.7, -25.12) * mm});
            skLineSegment(sketch, "E308", {"start": v(60.37, -26.94) * mm, "end": v(60.3, -28.81) * mm});
            skLineSegment(sketch, "E309", {"start": v(59.64, -29.53) * mm, "end": v(56.49, -30) * mm});
            skLineSegment(sketch, "E310", {"start": v(59.76, -26.17) * mm, "end": v(56.66, -25.52) * mm});
            skArc(sketch, "E311.filletArc", {"start": v(60.37, -26.94) * mm, "mid": v(60.2, -26.44) * mm, "end": v(59.76, -26.17) * mm});
            skArc(sketch, "E312.filletArc", {"start": v(59.64, -29.53) * mm, "mid": v(60.1, -29.29) * mm, "end": v(60.3, -28.81) * mm});
            skArc(sketch, "E313.filletArc", {"start": v(56.66, -25.52) * mm, "mid": v(56.04, -25.67) * mm, "end": v(55.75, -26.25) * mm});
            skLineSegment(sketch, "E314", {"start": v(55.75, -26.25) * mm, "end": v(55.62, -29.2) * mm});
            skArc(sketch, "E315.filletArc", {"start": v(55.62, -29.2) * mm, "mid": v(55.87, -29.8) * mm, "end": v(56.49, -30) * mm});
            skLineSegment(sketch, "E316", {"start": v(59.7, -32.99) * mm, "end": v(59.16, -34.7) * mm});
            skLineSegment(sketch, "E317", {"start": v(58.34, -35.24) * mm, "end": v(55, -34.85) * mm});
            skLineSegment(sketch, "E318", {"start": v(59.31, -32.08) * mm, "end": v(56.32, -30.58) * mm});
            skArc(sketch, "E319.filletArc", {"start": v(59.7, -32.99) * mm, "mid": v(59.67, -32.46) * mm, "end": v(59.31, -32.08) * mm});
            skArc(sketch, "E320.filletArc", {"start": v(58.34, -35.24) * mm, "mid": v(58.85, -35.12) * mm, "end": v(59.16, -34.7) * mm});
            skArc(sketch, "E321.filletArc", {"start": v(56.32, -30.58) * mm, "mid": v(55.68, -30.56) * mm, "end": v(55.25, -31.04) * mm});
            skLineSegment(sketch, "E322", {"start": v(55.25, -31.04) * mm, "end": v(54.36, -33.86) * mm});
            skArc(sketch, "E323.filletArc", {"start": v(54.36, -33.86) * mm, "mid": v(54.45, -34.5) * mm, "end": v(55, -34.85) * mm});
            skLineSegment(sketch, "E324", {"start": v(57.02, -38.74) * mm, "end": v(55.95, -40.27) * mm});
            skLineSegment(sketch, "E325", {"start": v(55.01, -40.52) * mm, "end": v(52.11, -39.2) * mm});
            skLineSegment(sketch, "E326", {"start": v(56.93, -37.75) * mm, "end": v(54.67, -35.54) * mm});
            skArc(sketch, "E327.filletArc", {"start": v(57.02, -38.74) * mm, "mid": v(57.16, -38.23) * mm, "end": v(56.93, -37.75) * mm});
            skArc(sketch, "E328.filletArc", {"start": v(55.01, -40.52) * mm, "mid": v(55.53, -40.56) * mm, "end": v(55.95, -40.27) * mm});
            skArc(sketch, "E329.filletArc", {"start": v(54.67, -35.54) * mm, "mid": v(54.06, -35.33) * mm, "end": v(53.5, -35.66) * mm});
            skLineSegment(sketch, "E330", {"start": v(53.5, -35.66) * mm, "end": v(51.8, -38.08) * mm});
            skArc(sketch, "E331.filletArc", {"start": v(51.8, -38.08) * mm, "mid": v(51.69, -38.72) * mm, "end": v(52.11, -39.2) * mm});
            skLineSegment(sketch, "E332", {"start": v(53.1, -43.7) * mm, "end": v(51.66, -44.9) * mm});
            skLineSegment(sketch, "E333", {"start": v(50.69, -44.91) * mm, "end": v(48.22, -42.9) * mm});
            skLineSegment(sketch, "E334", {"start": v(53.26, -42.74) * mm, "end": v(51.64, -40.01) * mm});
            skArc(sketch, "E335.filletArc", {"start": v(53.1, -43.7) * mm, "mid": v(53.35, -43.25) * mm, "end": v(53.26, -42.74) * mm});
            skArc(sketch, "E336.filletArc", {"start": v(50.69, -44.91) * mm, "mid": v(51.17, -45.09) * mm, "end": v(51.66, -44.9) * mm});
            skArc(sketch, "E337.filletArc", {"start": v(51.64, -40.01) * mm, "mid": v(51.11, -39.65) * mm, "end": v(50.5, -39.82) * mm});
            skLineSegment(sketch, "E338", {"start": v(50.5, -39.82) * mm, "end": v(48.22, -41.72) * mm});
            skArc(sketch, "E339.filletArc", {"start": v(48.22, -41.72) * mm, "mid": v(47.94, -42.3) * mm, "end": v(48.22, -42.9) * mm});
            skLineSegment(sketch, "E340", {"start": v(47.88, -47.52) * mm, "end": v(46.15, -48.24) * mm});
            skLineSegment(sketch, "E341", {"start": v(45.22, -47.95) * mm, "end": v(43.48, -45.28) * mm});
            skLineSegment(sketch, "E342", {"start": v(48.33, -46.65) * mm, "end": v(47.6, -43.57) * mm});
            skArc(sketch, "E343.filletArc", {"start": v(47.88, -47.52) * mm, "mid": v(48.27, -47.17) * mm, "end": v(48.33, -46.65) * mm});
            skArc(sketch, "E344.filletArc", {"start": v(45.22, -47.95) * mm, "mid": v(45.64, -48.26) * mm, "end": v(46.15, -48.24) * mm});
            skArc(sketch, "E345.filletArc", {"start": v(47.6, -43.57) * mm, "mid": v(47.21, -43.06) * mm, "end": v(46.57, -43.04) * mm});
            skLineSegment(sketch, "E346", {"start": v(46.57, -43.04) * mm, "end": v(43.83, -44.16) * mm});
            skArc(sketch, "E347.filletArc", {"start": v(43.83, -44.16) * mm, "mid": v(43.4, -44.64) * mm, "end": v(43.48, -45.28) * mm});
            skArc(sketch, "E348.MirrorCS", {"start": v(19.64, -22.21) * mm, "mid": v(20.22, -22.5) * mm, "end": v(20.37, -23.12) * mm});
            skArc(sketch, "E349.MirrorCS", {"start": v(19.83, -26.03) * mm, "mid": v(19.45, -26.56) * mm, "end": v(18.8, -26.6) * mm});
            skArc(sketch, "E350.MirrorCS", {"start": v(30.07, -10.55) * mm, "mid": v(29.42, -10.49) * mm, "end": v(29.06, -9.95) * mm});
            skArc(sketch, "E351.MirrorCS", {"start": v(24.93, -40.6) * mm, "mid": v(25.43, -40.2) * mm, "end": v(26.06, -40.33) * mm});
            skArc(sketch, "E352.MirrorCS", {"start": v(18.25, -36.58) * mm, "mid": v(17.74, -36.5) * mm, "end": v(17.4, -36.11) * mm});
            skArc(sketch, "E353.MirrorCS", {"start": v(16.7, -34.38) * mm, "mid": v(16.7, -33.85) * mm, "end": v(17.02, -33.44) * mm});
            skLineSegment(sketch, "E354.MirrorCS", {"start": v(16.7, -34.38) * mm, "end": v(17.4, -36.11) * mm});
            skArc(sketch, "E355.MirrorCS", {"start": v(24.67, -38.92) * mm, "mid": v(24.8, -39.55) * mm, "end": v(24.39, -40.06) * mm});
            skArc(sketch, "E356.MirrorCS", {"start": v(38, -45.15) * mm, "mid": v(38.58, -45.46) * mm, "end": v(38.7, -46.1) * mm});
            skArc(sketch, "E357.MirrorCS", {"start": v(23.1, -17.17) * mm, "mid": v(22.52, -17.46) * mm, "end": v(21.93, -17.2) * mm});
            skArc(sketch, "E358.MirrorCS", {"start": v(21.94, -34.94) * mm, "mid": v(21.9, -35.58) * mm, "end": v(21.38, -35.97) * mm});
            skArc(sketch, "E359.MirrorCS", {"start": v(28.47, -42.05) * mm, "mid": v(28.8, -42.61) * mm, "end": v(28.56, -43.22) * mm});
            skLineSegment(sketch, "E360.MirrorCS", {"start": v(24.93, -14.84) * mm, "end": v(23.1, -17.17) * mm});
            skLineSegment(sketch, "E361.MirrorCS", {"start": v(20.37, -23.12) * mm, "end": v(19.83, -26.03) * mm});
            skLineSegment(sketch, "E362.MirrorCS", {"start": v(26.06, -40.33) * mm, "end": v(28.47, -42.05) * mm});
            skArc(sketch, "E363.MirrorCS", {"start": v(34.25, -45.84) * mm, "mid": v(34.45, -45.23) * mm, "end": v(35.05, -45) * mm});
            skArc(sketch, "E364.MirrorCS", {"start": v(24.7, -13.7) * mm, "mid": v(25.09, -14.21) * mm, "end": v(24.93, -14.84) * mm});
            skArc(sketch, "E365.MirrorCS", {"start": v(19.73, -31.8) * mm, "mid": v(20.37, -31.74) * mm, "end": v(20.84, -32.19) * mm});
            skArc(sketch, "E366.MirrorCS", {"start": v(33.28, -8.48) * mm, "mid": v(33.32, -9.12) * mm, "end": v(32.86, -9.57) * mm});
            skArc(sketch, "E367.MirrorCS", {"start": v(37.95, -49.19) * mm, "mid": v(37.66, -49.62) * mm, "end": v(37.16, -49.77) * mm});
            skArc(sketch, "E368.MirrorCS", {"start": v(19.73, -14.67) * mm, "mid": v(19.54, -14.18) * mm, "end": v(19.7, -13.7) * mm});
            skArc(sketch, "E369.MirrorCS", {"start": v(15.84, -25.44) * mm, "mid": v(15.45, -25.1) * mm, "end": v(15.36, -24.6) * mm});
            skArc(sketch, "E370.MirrorCS", {"start": v(26.25, -45.42) * mm, "mid": v(25.78, -45.63) * mm, "end": v(25.28, -45.49) * mm});
            skArc(sketch, "E371.MirrorCS", {"start": v(28.58, -6.8) * mm, "mid": v(28.68, -6.3) * mm, "end": v(29.08, -5.97) * mm});
            skArc(sketch, "E372.MirrorCS", {"start": v(30.84, -5.35) * mm, "mid": v(31.37, -5.36) * mm, "end": v(31.77, -5.7) * mm});
            skArc(sketch, "E373.MirrorCS", {"start": v(23.76, -44.4) * mm, "mid": v(23.47, -43.96) * mm, "end": v(23.53, -43.44) * mm});
            skArc(sketch, "E374.MirrorCS", {"start": v(35.3, -49.66) * mm, "mid": v(34.82, -49.46) * mm, "end": v(34.58, -48.99) * mm});
            skArc(sketch, "E375.MirrorCS", {"start": v(15.71, -22.76) * mm, "mid": v(15.98, -22.3) * mm, "end": v(16.48, -22.14) * mm});
            skArc(sketch, "E376.MirrorCS", {"start": v(20.83, -12.27) * mm, "mid": v(21.28, -12) * mm, "end": v(21.8, -12.08) * mm});
            skLineSegment(sketch, "E377.MirrorCS", {"start": v(16.48, -22.14) * mm, "end": v(19.64, -22.21) * mm});
            skLineSegment(sketch, "E378.MirrorCS", {"start": v(21.8, -12.08) * mm, "end": v(24.7, -13.7) * mm});
            skLineSegment(sketch, "E379.MirrorCS", {"start": v(37.95, -49.19) * mm, "end": v(38.7, -46.1) * mm});
            skLineSegment(sketch, "E380.MirrorCS", {"start": v(26.25, -45.42) * mm, "end": v(28.56, -43.22) * mm});
            skLineSegment(sketch, "E381.MirrorCS", {"start": v(15.84, -25.44) * mm, "end": v(18.8, -26.6) * mm});
            skLineSegment(sketch, "E382.MirrorCS", {"start": v(23.76, -44.4) * mm, "end": v(25.28, -45.49) * mm});
            skLineSegment(sketch, "E383.MirrorCS", {"start": v(20.83, -12.27) * mm, "end": v(19.7, -13.7) * mm});
            skLineSegment(sketch, "E384.MirrorCS", {"start": v(35.3, -49.66) * mm, "end": v(37.16, -49.77) * mm});
            skLineSegment(sketch, "E385.MirrorCS", {"start": v(15.71, -22.76) * mm, "end": v(15.36, -24.6) * mm});
            skLineSegment(sketch, "E386.MirrorCS", {"start": v(30.84, -5.35) * mm, "end": v(29.08, -5.97) * mm});
            skArc(sketch, "E387.MirrorCS", {"start": v(20.37, -30.59) * mm, "mid": v(20.17, -31.2) * mm, "end": v(19.56, -31.44) * mm});
            skArc(sketch, "E388.MirrorCS", {"start": v(33.06, -44.3) * mm, "mid": v(33.51, -44.76) * mm, "end": v(33.44, -45.41) * mm});
            skArc(sketch, "E389.MirrorCS", {"start": v(26.12, -13.45) * mm, "mid": v(25.49, -13.59) * mm, "end": v(24.98, -13.18) * mm});
            skArc(sketch, "E390.MirrorCS", {"start": v(20.78, -21.48) * mm, "mid": v(20.31, -21.94) * mm, "end": v(19.67, -21.87) * mm});
            skLineSegment(sketch, "E391.MirrorCS", {"start": v(30.29, -43.26) * mm, "end": v(33.06, -44.3) * mm});
            skLineSegment(sketch, "E392.MirrorCS", {"start": v(28.48, -11.66) * mm, "end": v(26.12, -13.45) * mm});
            skLineSegment(sketch, "E393.MirrorCS", {"start": v(21.81, -18.71) * mm, "end": v(20.78, -21.48) * mm});
            skLineSegment(sketch, "E394.MirrorCS", {"start": v(25.28, -8.26) * mm, "end": v(23.79, -9.38) * mm});
            skArc(sketch, "E395.MirrorCS", {"start": v(19.03, -27) * mm, "mid": v(19.66, -27.1) * mm, "end": v(20, -27.65) * mm});
            skArc(sketch, "E396.MirrorCS", {"start": v(21.73, -36.46) * mm, "mid": v(22.33, -36.23) * mm, "end": v(22.9, -36.55) * mm});
            skArc(sketch, "E397.MirrorCS", {"start": v(29.26, -43.82) * mm, "mid": v(29.65, -43.3) * mm, "end": v(30.29, -43.26) * mm});
            skArc(sketch, "E398.MirrorCS", {"start": v(21.25, -17.69) * mm, "mid": v(21.77, -18.07) * mm, "end": v(21.81, -18.71) * mm});
            skArc(sketch, "E399.MirrorCS", {"start": v(28.55, -10.5) * mm, "mid": v(28.79, -11.1) * mm, "end": v(28.48, -11.66) * mm});
            skArc(sketch, "E400.MirrorCS", {"start": v(23.56, -10.33) * mm, "mid": v(23.5, -9.81) * mm, "end": v(23.79, -9.38) * mm});
            skArc(sketch, "E401.MirrorCS", {"start": v(16.38, -31.24) * mm, "mid": v(15.91, -31.04) * mm, "end": v(15.68, -30.58) * mm});
            skArc(sketch, "E402.MirrorCS", {"start": v(21.36, -41.53) * mm, "mid": v(20.85, -41.59) * mm, "end": v(20.42, -41.3) * mm});
            skArc(sketch, "E403.MirrorCS", {"start": v(31.79, -48.13) * mm, "mid": v(31.38, -48.45) * mm, "end": v(30.87, -48.45) * mm});
            skArc(sketch, "E404.MirrorCS", {"start": v(16.95, -20.21) * mm, "mid": v(16.62, -19.8) * mm, "end": v(16.63, -19.3) * mm});
            skArc(sketch, "E405.MirrorCS", {"start": v(15.45, -28.72) * mm, "mid": v(15.57, -28.2) * mm, "end": v(15.99, -27.9) * mm});
            skArc(sketch, "E406.MirrorCS", {"start": v(29.12, -47.79) * mm, "mid": v(28.72, -47.44) * mm, "end": v(28.64, -46.92) * mm});
            skArc(sketch, "E407.MirrorCS", {"start": v(19.34, -39.85) * mm, "mid": v(19.2, -39.35) * mm, "end": v(19.4, -38.87) * mm});
            skArc(sketch, "E408.MirrorCS", {"start": v(17.29, -17.54) * mm, "mid": v(17.63, -17.15) * mm, "end": v(18.15, -17.07) * mm});
            skArc(sketch, "E409.MirrorCS", {"start": v(25.28, -8.26) * mm, "mid": v(25.78, -8.1) * mm, "end": v(26.26, -8.31) * mm});
            skLineSegment(sketch, "E410.MirrorCS", {"start": v(16.95, -20.21) * mm, "end": v(19.67, -21.87) * mm});
            skLineSegment(sketch, "E411.MirrorCS", {"start": v(26.26, -8.31) * mm, "end": v(28.55, -10.5) * mm});
            skLineSegment(sketch, "E412.MirrorCS", {"start": v(28.64, -46.92) * mm, "end": v(29.26, -43.82) * mm});
            skLineSegment(sketch, "E413.MirrorCS", {"start": v(18.15, -17.07) * mm, "end": v(21.25, -17.69) * mm});
            skLineSegment(sketch, "E414.MirrorCS", {"start": v(17.29, -17.54) * mm, "end": v(16.63, -19.3) * mm});
            skLineSegment(sketch, "E415.MirrorCS", {"start": v(15.45, -28.72) * mm, "end": v(15.68, -30.58) * mm});
            skLineSegment(sketch, "E416.MirrorCS", {"start": v(19.34, -39.85) * mm, "end": v(20.42, -41.3) * mm});
            skLineSegment(sketch, "E417.MirrorCS", {"start": v(29.12, -47.79) * mm, "end": v(30.87, -48.45) * mm});
            skLineSegment(sketch, "E418.MirrorCS", {"start": v(18.25, -36.58) * mm, "end": v(21.38, -35.97) * mm});
            skLineSegment(sketch, "E419.MirrorCS", {"start": v(20, -27.65) * mm, "end": v(20.37, -30.59) * mm});
            skLineSegment(sketch, "E420.MirrorCS", {"start": v(22.9, -36.55) * mm, "end": v(24.67, -38.92) * mm});
            skLineSegment(sketch, "E421.MirrorCS", {"start": v(31.79, -48.13) * mm, "end": v(33.44, -45.41) * mm});
            skLineSegment(sketch, "E422.MirrorCS", {"start": v(19.4, -38.87) * mm, "end": v(21.73, -36.46) * mm});
            skLineSegment(sketch, "E423.MirrorCS", {"start": v(35.05, -45) * mm, "end": v(38, -45.15) * mm});
            skLineSegment(sketch, "E424.MirrorCS", {"start": v(20.84, -32.19) * mm, "end": v(21.94, -34.94) * mm});
            skLineSegment(sketch, "E425.MirrorCS", {"start": v(32.86, -9.57) * mm, "end": v(30.07, -10.55) * mm});
            skLineSegment(sketch, "E426.MirrorCS", {"start": v(31.77, -5.7) * mm, "end": v(33.28, -8.48) * mm});
            skLineSegment(sketch, "E427.MirrorCS", {"start": v(17.02, -33.44) * mm, "end": v(19.73, -31.8) * mm});
            skLineSegment(sketch, "E428.MirrorCS", {"start": v(23.53, -43.44) * mm, "end": v(24.93, -40.6) * mm});
            skLineSegment(sketch, "E429.MirrorCS", {"start": v(34.58, -48.99) * mm, "end": v(34.25, -45.84) * mm});
            skLineSegment(sketch, "E430.MirrorCS", {"start": v(19.73, -14.67) * mm, "end": v(21.93, -17.2) * mm});
            skLineSegment(sketch, "E431.MirrorCS", {"start": v(28.58, -6.8) * mm, "end": v(29.06, -9.95) * mm});
            skLineSegment(sketch, "E432.MirrorCS", {"start": v(23.56, -10.33) * mm, "end": v(24.98, -13.18) * mm});
            skLineSegment(sketch, "E433.MirrorCS", {"start": v(16.38, -31.24) * mm, "end": v(19.56, -31.44) * mm});
            skLineSegment(sketch, "E434.MirrorCS", {"start": v(21.36, -41.53) * mm, "end": v(24.39, -40.06) * mm});
            skLineSegment(sketch, "E435.MirrorCS", {"start": v(15.99, -27.9) * mm, "end": v(19.03, -27) * mm});
            skLineSegment(sketch, "E436", {"start": v(42.73, -49.01) * mm, "end": v(40.9, -49.34) * mm});
            skLineSegment(sketch, "E437", {"start": v(40.05, -48.86) * mm, "end": v(38.92, -45.88) * mm});
            skLineSegment(sketch, "E438", {"start": v(43.36, -48.25) * mm, "end": v(43.32, -45.1) * mm});
            skArc(sketch, "E439.filletArc", {"start": v(42.73, -49.01) * mm, "mid": v(43.18, -48.75) * mm, "end": v(43.36, -48.25) * mm});
            skArc(sketch, "E440.filletArc", {"start": v(40.05, -48.86) * mm, "mid": v(40.38, -49.25) * mm, "end": v(40.9, -49.34) * mm});
            skArc(sketch, "E441.filletArc", {"start": v(43.32, -45.1) * mm, "mid": v(43.04, -44.5) * mm, "end": v(42.42, -44.35) * mm});
            skLineSegment(sketch, "E442", {"start": v(42.42, -44.35) * mm, "end": v(39.5, -44.86) * mm});
            skArc(sketch, "E443.filletArc", {"start": v(39.5, -44.86) * mm, "mid": v(38.97, -45.23) * mm, "end": v(38.92, -45.88) * mm});
            skLineSegment(sketch, "E444", {"start": v(36.86, -4.4) * mm, "end": v(38.72, -4.4) * mm});
            skLineSegment(sketch, "E445", {"start": v(39.47, -5.02) * mm, "end": v(40.06, -8.15) * mm});
            skLineSegment(sketch, "E446", {"start": v(36.1, -5.04) * mm, "end": v(35.6, -8.16) * mm});
            skArc(sketch, "E447.filletArc", {"start": v(36.86, -4.4) * mm, "mid": v(36.36, -4.58) * mm, "end": v(36.1, -5.04) * mm});
            skArc(sketch, "E448.filletArc", {"start": v(39.47, -5.02) * mm, "mid": v(39.21, -4.57) * mm, "end": v(38.72, -4.4) * mm});
            skArc(sketch, "E449.filletArc", {"start": v(35.6, -8.16) * mm, "mid": v(35.77, -8.78) * mm, "end": v(36.35, -9.04) * mm});
            skLineSegment(sketch, "E450", {"start": v(36.35, -9.04) * mm, "end": v(39.31, -9.05) * mm});
            skArc(sketch, "E451.filletArc", {"start": v(39.31, -9.05) * mm, "mid": v(39.9, -8.78) * mm, "end": v(40.06, -8.15) * mm});
            skSolve(sketch);
        }
        {
            var Q0;
            Q0=makeQuery(id+"F0.imprint","IMPRINT",FACE,{"disambiguationData":[TD([[makeQuery(id+"F0.imprint","IMPRINT",EDGE,{"derivedFrom":sQuery(id+"F0.wireOp",EDGE,"E55")}),1.0]])]});
            var Q1;
            Q1=makeQuery(id+"F0.imprint","IMPRINT",FACE,{"disambiguationData":[TD([[makeQuery(id+"F0.imprint","IMPRINT",EDGE,{"derivedFrom":sQuery(id+"F0.wireOp",EDGE,"E116")}),-1.0]])]});
            var Q2;
            Q2=makeQuery(id+"F0.imprint","IMPRINT",FACE,{"disambiguationData":[TD([[makeQuery(id+"F0.imprint","IMPRINT",EDGE,{"derivedFrom":sQuery(id+"F0.wireOp",EDGE,"E63")}),1.0]])]});
            var Q3;
            {var subQ2=sQuery(id+"F0.wireOp",EDGE,"E133.MirrorCS");Q3=makeQuery(id+"F0.imprint","IMPRINT",FACE,{"disambiguationData":[TD([[makeQuery(id+"F0.imprint","IMPRINT",EDGE,{"derivedFrom":subQ2}),-1.0]])]});}
            var Q4;
            Q4=makeQuery(id+"F0.imprint","IMPRINT",FACE,{"disambiguationData":[TD([[makeQuery(id+"F0.imprint","IMPRINT",EDGE,{"derivedFrom":sQuery(id+"F0.wireOp",EDGE,"E47")}),1.0]])]});
            var Q5;
            Q5=makeQuery(id+"F0.imprint","IMPRINT",FACE,{"disambiguationData":[TD([[makeQuery(id+"F0.imprint","IMPRINT",EDGE,{"derivedFrom":sQuery(id+"F0.wireOp",EDGE,"E108")}),-1.0]])]});
            var Q6;
            {var subQ0=sQuery(id+"F0.wireOp",EDGE,"LEBjBg5W-HPN8-HCAC-WDjT-1sEjF4hljOFS");var subQ1=sQuery(id+"F0.wireOp",EDGE,"E1");var subQ2=makeQuery(id+"F0.imprint","INTERSECT",VERTEX,{"disambiguationData":[OD(0.0)],"derivedFrom":[subQ1,subQ0]});Q6=makeQuery(id+"F0.imprint","IMPRINT",FACE,{"disambiguationData":[TD([[makeQuery(id+"F0.imprint","IMPRINT",EDGE,{"disambiguationData":[TD([[subQ2,-1.0]])],"derivedFrom":subQ1}),1.0]])]});}
            var Q7;
            {var subQ5=sQuery(id+"F0.wireOp",EDGE,"E199.MirrorCS");Q7=makeQuery(id+"F0.imprint","IMPRINT",FACE,{"disambiguationData":[TD([[makeQuery(id+"F0.imprint","IMPRINT",EDGE,{"derivedFrom":subQ5}),-1.0]])]});}
            var Q8;
            Q8=makeQuery(id+"F0.imprint","IMPRINT",FACE,{"disambiguationData":[TD([[makeQuery(id+"F0.imprint","IMPRINT",EDGE,{"derivedFrom":sQuery(id+"F0.wireOp",EDGE,"E39")}),1.0]])]});
            var Q9;
            Q9=makeQuery(id+"F0.imprint","IMPRINT",FACE,{"disambiguationData":[TD([[makeQuery(id+"F0.imprint","IMPRINT",EDGE,{"derivedFrom":sQuery(id+"F0.wireOp",EDGE,"E100")}),-1.0]])]});
            var Q10;
            {var subQ0=sQuery(id+"F0.wireOp",EDGE,"LEBjBg5W-HPN8-HCAC-WDjT-1sEjF4hljOFS");var subQ1=sQuery(id+"F0.wireOp",EDGE,"E1");var subQ2=makeQuery(id+"F0.imprint","INTERSECT",VERTEX,{"disambiguationData":[OD(0.0)],"derivedFrom":[subQ1,subQ0]});Q10=makeQuery(id+"F0.imprint","IMPRINT",FACE,{"disambiguationData":[TD([[makeQuery(id+"F0.imprint","IMPRINT",EDGE,{"disambiguationData":[TD([[subQ2,1.0]])],"derivedFrom":subQ1}),1.0]])]});}
            var Q11;
            Q11=makeQuery(id+"F0.imprint","IMPRINT",FACE,{"disambiguationData":[TD([[makeQuery(id+"F0.imprint","IMPRINT",EDGE,{"derivedFrom":sQuery(id+"F0.wireOp",EDGE,"E76")}),-1.0]])]});
            var Q12;
            {var subQ2=sQuery(id+"F0.wireOp",EDGE,"E147.MirrorCS");Q12=makeQuery(id+"F0.imprint","IMPRINT",FACE,{"disambiguationData":[TD([[makeQuery(id+"F0.imprint","IMPRINT",EDGE,{"derivedFrom":subQ2}),-1.0]])]});}
            var Q13;
            Q13=makeQuery(id+"F0.imprint","IMPRINT",FACE,{"disambiguationData":[TD([[makeQuery(id+"F0.imprint","IMPRINT",EDGE,{"derivedFrom":sQuery(id+"F0.wireOp",EDGE,"E15")}),1.0]])]});
            var Q14;
            Q14=makeQuery(id+"F0.imprint","IMPRINT",FACE,{"disambiguationData":[TD([[makeQuery(id+"F0.imprint","IMPRINT",EDGE,{"derivedFrom":sQuery(id+"F0.wireOp",EDGE,"E31")}),1.0]])]});
            var Q15;
            Q15=makeQuery(id+"F0.imprint","IMPRINT",FACE,{"disambiguationData":[TD([[makeQuery(id+"F0.imprint","IMPRINT",EDGE,{"derivedFrom":sQuery(id+"F0.wireOp",EDGE,"E92")}),-1.0]])]});
            var Q16;
            {var subQ4=sQuery(id+"F0.wireOp",EDGE,"E132.MirrorCS");Q16=makeQuery(id+"F0.imprint","IMPRINT",FACE,{"disambiguationData":[TD([[makeQuery(id+"F0.imprint","IMPRINT",EDGE,{"derivedFrom":subQ4}),-1.0]])]});}
            var Q17;
            Q17=makeQuery(id+"F0.imprint","IMPRINT",FACE,{"disambiguationData":[TD([[makeQuery(id+"F0.imprint","IMPRINT",EDGE,{"derivedFrom":sQuery(id+"F0.wireOp",EDGE,"E23")}),1.0]])]});
            var Q18;
            Q18=makeQuery(id+"F0.imprint","IMPRINT",FACE,{"disambiguationData":[TD([[makeQuery(id+"F0.imprint","IMPRINT",EDGE,{"derivedFrom":sQuery(id+"F0.wireOp",EDGE,"E84")}),-1.0]])]});
            var Q19;
            Q19=makeQuery(id+"F0.imprint","IMPRINT",FACE,{"disambiguationData":[TD([[makeQuery(id+"F0.imprint","IMPRINT",EDGE,{"derivedFrom":sQuery(id+"F0.wireOp",EDGE,"E187.MirrorCS")}),-1.0]])]});
            var Q20;
            Q20=makeQuery(id+"F0.imprint","IMPRINT",FACE,{"disambiguationData":[TD([[makeQuery(id+"F0.imprint","IMPRINT",EDGE,{"derivedFrom":sQuery(id+"F0.wireOp",EDGE,"E7")}),1.0]])]});
            var Q21;
            Q21=makeQuery(id+"F0.imprint","IMPRINT",FACE,{"disambiguationData":[TD([[makeQuery(id+"F0.imprint","IMPRINT",EDGE,{"derivedFrom":sQuery(id+"F0.wireOp",EDGE,"E68")}),-1.0]])]});
            var Q22;
            Q22=makeQuery(id+"F0.imprint","IMPRINT",FACE,{"disambiguationData":[TD([[makeQuery(id+"F0.imprint","IMPRINT",EDGE,{"derivedFrom":sQuery(id+"F0.wireOp",EDGE,"E138.MirrorCS")}),-1.0]])]});
            var Q23;
            {var subQ1=sQuery(id+"F0.wireOp",EDGE,"E234.MirrorCS");Q23=makeQuery(id+"F0.imprint","IMPRINT",FACE,{"disambiguationData":[TD([[makeQuery(id+"F0.imprint","IMPRINT",EDGE,{"derivedFrom":subQ1}),-1.0]])]});}
            var Q24;
            Q24=makeQuery(id+"F0.imprint","IMPRINT",FACE,{"disambiguationData":[TD([[makeQuery(id+"F0.imprint","IMPRINT",EDGE,{"derivedFrom":sQuery(id+"F0.wireOp",EDGE,"E252")}),-1.0]])]});
            var Q25;
            Q25=makeQuery(id+"F0.imprint","IMPRINT",FACE,{"disambiguationData":[TD([[makeQuery(id+"F0.imprint","IMPRINT",EDGE,{"derivedFrom":sQuery(id+"F0.wireOp",EDGE,"E60")}),-1.0]])]});
            var Q26;
            Q26=makeQuery(id+"F0.imprint","IMPRINT",FACE,{"disambiguationData":[TD([[makeQuery(id+"F0.imprint","IMPRINT",EDGE,{"derivedFrom":sQuery(id+"F0.wireOp",EDGE,"E188.MirrorCS")}),-1.0]])]});
            var Q27;
            Q27=makeQuery(id+"F0.imprint","IMPRINT",FACE,{"disambiguationData":[TD([[makeQuery(id+"F0.imprint","IMPRINT",EDGE,{"derivedFrom":sQuery(id+"F0.wireOp",EDGE,"E127")}),1.0]])]});
            var Q28;
            {var subQ0=sQuery(id+"F0.wireOp",EDGE,"E263");Q28=makeQuery(id+"F0.imprint","IMPRINT",FACE,{"disambiguationData":[TD([[makeQuery(id+"F0.imprint","IMPRINT",EDGE,{"derivedFrom":subQ0}),1.0]])]});}
            var Q29;
            Q29=makeQuery(id+"F0.imprint","IMPRINT",FACE,{"disambiguationData":[TD([[makeQuery(id+"F0.imprint","IMPRINT",EDGE,{"derivedFrom":sQuery(id+"F0.wireOp",EDGE,"E163.MirrorCS")}),-1.0]])]});
            var Q30;
            Q30=makeQuery(id+"F0.imprint","IMPRINT",FACE,{"disambiguationData":[TD([[makeQuery(id+"F0.imprint","IMPRINT",EDGE,{"derivedFrom":sQuery(id+"F0.wireOp",EDGE,"E119")}),1.0]])]});
            var Q31;
            Q31=makeQuery(id+"F0.imprint","IMPRINT",FACE,{"disambiguationData":[TD([[makeQuery(id+"F0.imprint","IMPRINT",EDGE,{"derivedFrom":sQuery(id+"F0.wireOp",EDGE,"E189.MirrorCS")}),-1.0]])]});
            var Q32;
            Q32=makeQuery(id+"F0.imprint","IMPRINT",FACE,{"disambiguationData":[TD([[makeQuery(id+"F0.imprint","IMPRINT",EDGE,{"derivedFrom":sQuery(id+"F0.wireOp",EDGE,"E111")}),1.0]])]});
            var Q33;
            {var subQ0=sQuery(id+"F0.wireOp",EDGE,"E227.MirrorCS");Q33=makeQuery(id+"F0.imprint","IMPRINT",FACE,{"disambiguationData":[TD([[makeQuery(id+"F0.imprint","IMPRINT",EDGE,{"derivedFrom":subQ0}),-1.0]])]});}
            var Q34;
            Q34=makeQuery(id+"F0.imprint","IMPRINT",FACE,{"disambiguationData":[TD([[makeQuery(id+"F0.imprint","IMPRINT",EDGE,{"derivedFrom":sQuery(id+"F0.wireOp",EDGE,"E103")}),1.0]])]});
            var Q35;
            Q35=makeQuery(id+"F0.imprint","IMPRINT",FACE,{"disambiguationData":[TD([[makeQuery(id+"F0.imprint","IMPRINT",EDGE,{"derivedFrom":sQuery(id+"F0.wireOp",EDGE,"E7")}),-1.0]])]});
            var Q36;
            Q36=makeQuery(id+"F0.imprint","IMPRINT",FACE,{"disambiguationData":[TD([[makeQuery(id+"F0.imprint","IMPRINT",EDGE,{"derivedFrom":sQuery(id+"F0.wireOp",EDGE,"E95")}),1.0]])]});
            var Q37;
            {var subQ6=sQuery(id+"F0.wireOp",EDGE,"E145.MirrorCS");Q37=makeQuery(id+"F0.imprint","IMPRINT",FACE,{"disambiguationData":[TD([[makeQuery(id+"F0.imprint","IMPRINT",EDGE,{"derivedFrom":subQ6}),-1.0]])]});}
            var Q38;
            Q38=makeQuery(id+"F0.imprint","IMPRINT",FACE,{"disambiguationData":[TD([[makeQuery(id+"F0.imprint","IMPRINT",EDGE,{"derivedFrom":sQuery(id+"F0.wireOp",EDGE,"E135.MirrorCS")}),-1.0]])]});
            var Q39;
            Q39=makeQuery(id+"F0.imprint","IMPRINT",FACE,{"disambiguationData":[TD([[makeQuery(id+"F0.imprint","IMPRINT",EDGE,{"derivedFrom":sQuery(id+"F0.wireOp",EDGE,"E166.MirrorCS")}),-1.0]])]});
            var Q40;
            Q40=makeQuery(id+"F0.imprint","IMPRINT",FACE,{"disambiguationData":[TD([[makeQuery(id+"F0.imprint","IMPRINT",EDGE,{"derivedFrom":sQuery(id+"F0.wireOp",EDGE,"E190.MirrorCS")}),-1.0]])]});
            var Q41;
            Q41=makeQuery(id+"F0.imprint","IMPRINT",FACE,{"disambiguationData":[TD([[makeQuery(id+"F0.imprint","IMPRINT",EDGE,{"derivedFrom":sQuery(id+"F0.wireOp",EDGE,"E52")}),-1.0]])]});
            var Q42;
            Q42=makeQuery(id+"F0.imprint","IMPRINT",FACE,{"disambiguationData":[TD([[makeQuery(id+"F0.imprint","IMPRINT",EDGE,{"derivedFrom":sQuery(id+"F0.wireOp",EDGE,"E44")}),-1.0]])]});
            var Q43;
            Q43=makeQuery(id+"F0.imprint","IMPRINT",FACE,{"disambiguationData":[TD([[makeQuery(id+"F0.imprint","IMPRINT",EDGE,{"derivedFrom":sQuery(id+"F0.wireOp",EDGE,"E36")}),-1.0]])]});
            var Q44;
            Q44=makeQuery(id+"F0.imprint","IMPRINT",FACE,{"disambiguationData":[TD([[makeQuery(id+"F0.imprint","IMPRINT",EDGE,{"derivedFrom":sQuery(id+"F0.wireOp",EDGE,"E28")}),-1.0]])]});
            var Q45;
            Q45=makeQuery(id+"F0.imprint","IMPRINT",FACE,{"disambiguationData":[TD([[makeQuery(id+"F0.imprint","IMPRINT",EDGE,{"derivedFrom":sQuery(id+"F0.wireOp",EDGE,"E20")}),-1.0]])]});
            var Q46;
            Q46=makeQuery(id+"F0.imprint","IMPRINT",FACE,{"disambiguationData":[TD([[makeQuery(id+"F0.imprint","IMPRINT",EDGE,{"derivedFrom":sQuery(id+"F0.wireOp",EDGE,"E12")}),-1.0]])]});
            var Q47;
            Q47=makeQuery(id+"F0.imprint","IMPRINT",FACE,{"disambiguationData":[TD([[makeQuery(id+"F0.imprint","IMPRINT",EDGE,{"derivedFrom":sQuery(id+"F0.wireOp",EDGE,"E4")}),-1.0]])]});
            var Q48;
            Q48=makeQuery(id+"F0.imprint","IMPRINT",FACE,{"disambiguationData":[TD([[makeQuery(id+"F0.imprint","IMPRINT",EDGE,{"derivedFrom":sQuery(id+"F0.wireOp",EDGE,"E260")}),-1.0]])]});
            var Q49;
            {var subQ1=sQuery(id+"F0.wireOp",EDGE,"E251.MirrorCS");Q49=makeQuery(id+"F0.imprint","IMPRINT",FACE,{"disambiguationData":[TD([[makeQuery(id+"F0.imprint","IMPRINT",EDGE,{"derivedFrom":subQ1}),-1.0]])]});}
            var Q50;
            Q50=makeQuery(id+"F0.imprint","IMPRINT",FACE,{"disambiguationData":[TD([[makeQuery(id+"F0.imprint","IMPRINT",EDGE,{"derivedFrom":sQuery(id+"F0.wireOp",EDGE,"E165.MirrorCS")}),-1.0]])]});
            var Q51;
            Q51=makeQuery(id+"F0.imprint","IMPRINT",FACE,{"disambiguationData":[TD([[makeQuery(id+"F0.imprint","IMPRINT",EDGE,{"derivedFrom":sQuery(id+"F0.wireOp",EDGE,"E144.MirrorCS")}),-1.0]])]});
            var Q52;
            {var subQ2=sQuery(id+"F0.wireOp",EDGE,"E164.MirrorCS");Q52=makeQuery(id+"F0.imprint","IMPRINT",FACE,{"disambiguationData":[TD([[makeQuery(id+"F0.imprint","IMPRINT",EDGE,{"derivedFrom":subQ2}),-1.0]])]});}
            var Q53;
            {var subQ94=sQuery(id+"F0.wireOp",EDGE,"E234.MirrorCS");Q53=makeQuery(id+"F0.imprint","IMPRINT",FACE,{"disambiguationData":[TD([[makeQuery(id+"F0.imprint","IMPRINT",EDGE,{"derivedFrom":subQ94}),1.0]])]});}
            var Q54;
            Q54=makeQuery(id+"F0.imprint","IMPRINT",FACE,{"disambiguationData":[TD([[makeQuery(id+"F0.imprint","IMPRINT",EDGE,{"derivedFrom":sQuery(id+"F0.wireOp",EDGE,"E87")}),1.0]])]});
            var Q55;
            {var subQ1=sQuery(id+"F0.wireOp",EDGE,"E232.MirrorCS");Q55=makeQuery(id+"F0.imprint","IMPRINT",FACE,{"disambiguationData":[TD([[makeQuery(id+"F0.imprint","IMPRINT",EDGE,{"derivedFrom":subQ1}),-1.0]])]});}
            var Q56;
            Q56=makeQuery(id+"F0.imprint","IMPRINT",FACE,{"disambiguationData":[TD([[makeQuery(id+"F0.imprint","IMPRINT",EDGE,{"derivedFrom":sQuery(id+"F0.wireOp",EDGE,"E79")}),1.0]])]});
            var Q57;
            Q57=makeQuery(id+"F0.imprint","IMPRINT",FACE,{"disambiguationData":[TD([[makeQuery(id+"F0.imprint","IMPRINT",EDGE,{"derivedFrom":sQuery(id+"F0.wireOp",EDGE,"E124")}),-1.0]])]});
            var Q58;
            Q58=makeQuery(id+"F0.imprint","IMPRINT",FACE,{"disambiguationData":[TD([[makeQuery(id+"F0.imprint","IMPRINT",EDGE,{"derivedFrom":sQuery(id+"F0.wireOp",EDGE,"E71")}),1.0]])]});
            var Q59;
            {var subQ5=sQuery(id+"F0.wireOp",EDGE,"E170.MirrorCS");Q59=makeQuery(id+"F0.imprint","IMPRINT",FACE,{"disambiguationData":[TD([[makeQuery(id+"F0.imprint","IMPRINT",EDGE,{"derivedFrom":subQ5}),-1.0]])]});}
            var Q60;
            {var subQ4=sQuery(id+"F0.wireOp",EDGE,"E200.MirrorCS");Q60=makeQuery(id+"F0.imprint","IMPRINT",FACE,{"disambiguationData":[TD([[makeQuery(id+"F0.imprint","IMPRINT",EDGE,{"derivedFrom":subQ4}),-1.0]])]});}
            var Q61;
            {var subQ1=sQuery(id+"F0.wireOp",EDGE,"E153.MirrorCS");Q61=makeQuery(id+"F0.imprint","IMPRINT",FACE,{"disambiguationData":[TD([[makeQuery(id+"F0.imprint","IMPRINT",EDGE,{"derivedFrom":subQ1}),-1.0]])]});}
            var Q62;
            {var subQ1=sQuery(id+"F0.wireOp",EDGE,"E150.MirrorCS");Q62=makeQuery(id+"F0.imprint","IMPRINT",FACE,{"disambiguationData":[TD([[makeQuery(id+"F0.imprint","IMPRINT",EDGE,{"derivedFrom":subQ1}),-1.0]])]});}
            var Q63;
            {var subQ1=sQuery(id+"F0.wireOp",EDGE,"E149.MirrorCS");Q63=makeQuery(id+"F0.imprint","IMPRINT",FACE,{"disambiguationData":[TD([[makeQuery(id+"F0.imprint","IMPRINT",EDGE,{"derivedFrom":subQ1}),-1.0]])]});}
            var Q64;
            {var subQ0=sQuery(id+"F0.wireOp",EDGE,"E258.filletArc");Q64=makeQuery(id+"F0.imprint","IMPRINT",FACE,{"disambiguationData":[TD([[makeQuery(id+"F0.imprint","IMPRINT",EDGE,{"derivedFrom":subQ0}),1.0]])]});}
            var Q65;
            {var subQ0=sQuery(id+"F0.wireOp",EDGE,"LEBjBg5W-HPN8-HCAC-WDjT-1sEjF4hljOFS");var subQ1=sQuery(id+"F0.wireOp",EDGE,"E0");var subQ2=makeQuery(id+"F0.imprint","INTERSECT",VERTEX,{"disambiguationData":[OD(1.0)],"derivedFrom":[subQ1,subQ0]});Q65=makeQuery(id+"F0.imprint","IMPRINT",FACE,{"disambiguationData":[TD([[makeQuery(id+"F0.imprint","IMPRINT",EDGE,{"disambiguationData":[TD([[subQ2,-1.0]])],"derivedFrom":subQ1}),1.0]])]});}
            var Q66;
            {var subQ5=sQuery(id+"F0.wireOp",EDGE,"E174.MirrorCS");Q66=makeQuery(id+"F0.imprint","IMPRINT",FACE,{"disambiguationData":[TD([[makeQuery(id+"F0.imprint","IMPRINT",EDGE,{"derivedFrom":subQ5}),-1.0]])]});}
            var Q67;
            {var subQ5=sQuery(id+"F0.wireOp",EDGE,"E204.MirrorCS");Q67=makeQuery(id+"F0.imprint","IMPRINT",FACE,{"disambiguationData":[TD([[makeQuery(id+"F0.imprint","IMPRINT",EDGE,{"derivedFrom":subQ5}),-1.0]])]});}
            var Q68;
            {var subQ5=sQuery(id+"F0.wireOp",EDGE,"E175.MirrorCS");Q68=makeQuery(id+"F0.imprint","IMPRINT",FACE,{"disambiguationData":[TD([[makeQuery(id+"F0.imprint","IMPRINT",EDGE,{"derivedFrom":subQ5}),-1.0]])]});}
            var Q69;
            {var subQ5=sQuery(id+"F0.wireOp",EDGE,"E197.MirrorCS");Q69=makeQuery(id+"F0.imprint","IMPRINT",FACE,{"disambiguationData":[TD([[makeQuery(id+"F0.imprint","IMPRINT",EDGE,{"derivedFrom":subQ5}),-1.0]])]});}
            var Q70;
            {var subQ5=sQuery(id+"F0.wireOp",EDGE,"E202.MirrorCS");Q70=makeQuery(id+"F0.imprint","IMPRINT",FACE,{"disambiguationData":[TD([[makeQuery(id+"F0.imprint","IMPRINT",EDGE,{"derivedFrom":subQ5}),-1.0]])]});}
            var Q71;
            Q71=makeQuery(id+"F0.imprint","IMPRINT",FACE,{"disambiguationData":[TD([[makeQuery(id+"F0.imprint","IMPRINT",EDGE,{"derivedFrom":sQuery(id+"F0.wireOp",EDGE,"uwi4dv5m-cRki-Ywr8-IbC3-VpDon0NVQ4K6")}),-1.0]])]});
            var Q72;
            {var subQ1=sQuery(id+"F0.wireOp",EDGE,"E402.MirrorCS");Q72=makeQuery(id+"F0.imprint","IMPRINT",FACE,{"disambiguationData":[TD([[makeQuery(id+"F0.imprint","IMPRINT",EDGE,{"derivedFrom":subQ1}),-1.0]])]});}
            var Q73;
            {var subQ1=sQuery(id+"F0.wireOp",EDGE,"E370.MirrorCS");Q73=makeQuery(id+"F0.imprint","IMPRINT",FACE,{"disambiguationData":[TD([[makeQuery(id+"F0.imprint","IMPRINT",EDGE,{"derivedFrom":subQ1}),-1.0]])]});}
            var Q74;
            {var subQ5=sQuery(id+"F0.wireOp",EDGE,"E403.MirrorCS");Q74=makeQuery(id+"F0.imprint","IMPRINT",FACE,{"disambiguationData":[TD([[makeQuery(id+"F0.imprint","IMPRINT",EDGE,{"derivedFrom":subQ5}),-1.0]])]});}
            var Q75;
            Q75=makeQuery(id+"F0.imprint","IMPRINT",FACE,{"disambiguationData":[TD([[makeQuery(id+"F0.imprint","IMPRINT",EDGE,{"derivedFrom":sQuery(id+"F0.wireOp",EDGE,"E292")}),-1.0]])]});
            var Q76;
            Q76=makeQuery(id+"F0.imprint","IMPRINT",FACE,{"disambiguationData":[TD([[makeQuery(id+"F0.imprint","IMPRINT",EDGE,{"derivedFrom":sQuery(id+"F0.wireOp",EDGE,"E340")}),-1.0]])]});
            var Q77;
            Q77=makeQuery(id+"F0.imprint","IMPRINT",FACE,{"disambiguationData":[TD([[makeQuery(id+"F0.imprint","IMPRINT",EDGE,{"derivedFrom":sQuery(id+"F0.wireOp",EDGE,"E284")}),-1.0]])]});
            var Q78;
            Q78=makeQuery(id+"F0.imprint","IMPRINT",FACE,{"disambiguationData":[TD([[makeQuery(id+"F0.imprint","IMPRINT",EDGE,{"derivedFrom":sQuery(id+"F0.wireOp",EDGE,"E332")}),-1.0]])]});
            var Q79;
            Q79=makeQuery(id+"F0.imprint","IMPRINT",FACE,{"disambiguationData":[TD([[makeQuery(id+"F0.imprint","IMPRINT",EDGE,{"derivedFrom":sQuery(id+"F0.wireOp",EDGE,"E276")}),-1.0]])]});
            var Q80;
            Q80=makeQuery(id+"F0.imprint","IMPRINT",FACE,{"disambiguationData":[TD([[makeQuery(id+"F0.imprint","IMPRINT",EDGE,{"derivedFrom":sQuery(id+"F0.wireOp",EDGE,"E324")}),-1.0]])]});
            var Q81;
            Q81=makeQuery(id+"F0.imprint","IMPRINT",FACE,{"disambiguationData":[TD([[makeQuery(id+"F0.imprint","IMPRINT",EDGE,{"derivedFrom":sQuery(id+"F0.wireOp",EDGE,"E316")}),-1.0]])]});
            var Q82;
            Q82=makeQuery(id+"F0.imprint","IMPRINT",FACE,{"disambiguationData":[TD([[makeQuery(id+"F0.imprint","IMPRINT",EDGE,{"derivedFrom":sQuery(id+"F0.wireOp",EDGE,"E444")}),-1.0]])]});
            var Q83;
            Q83=makeQuery(id+"F0.imprint","IMPRINT",FACE,{"disambiguationData":[TD([[makeQuery(id+"F0.imprint","IMPRINT",EDGE,{"derivedFrom":sQuery(id+"F0.wireOp",EDGE,"E308")}),-1.0]])]});
            var Q84;
            Q84=makeQuery(id+"F0.imprint","IMPRINT",FACE,{"disambiguationData":[TD([[makeQuery(id+"F0.imprint","IMPRINT",EDGE,{"derivedFrom":sQuery(id+"F0.wireOp",EDGE,"E371.MirrorCS")}),-1.0]])]});
            var Q85;
            Q85=makeQuery(id+"F0.imprint","IMPRINT",FACE,{"disambiguationData":[TD([[makeQuery(id+"F0.imprint","IMPRINT",EDGE,{"derivedFrom":sQuery(id+"F0.wireOp",EDGE,"E3")}),-1.0]])]});
            var Q86;
            Q86=makeQuery(id+"F0.imprint","IMPRINT",FACE,{"disambiguationData":[TD([[makeQuery(id+"F0.imprint","IMPRINT",EDGE,{"derivedFrom":sQuery(id+"F0.wireOp",EDGE,"E394.MirrorCS")}),1.0]])]});
            var Q87;
            {var subQ1=sQuery(id+"F0.wireOp",EDGE,"E368.MirrorCS");Q87=makeQuery(id+"F0.imprint","IMPRINT",FACE,{"disambiguationData":[TD([[makeQuery(id+"F0.imprint","IMPRINT",EDGE,{"derivedFrom":subQ1}),-1.0]])]});}
            var Q88;
            Q88=makeQuery(id+"F0.imprint","IMPRINT",FACE,{"disambiguationData":[TD([[makeQuery(id+"F0.imprint","IMPRINT",EDGE,{"derivedFrom":sQuery(id+"F0.wireOp",EDGE,"E404.MirrorCS")}),-1.0]])]});
            var Q89;
            {var subQ1=sQuery(id+"F0.wireOp",EDGE,"E401.MirrorCS");Q89=makeQuery(id+"F0.imprint","IMPRINT",FACE,{"disambiguationData":[TD([[makeQuery(id+"F0.imprint","IMPRINT",EDGE,{"derivedFrom":subQ1}),-1.0]])]});}
            var Q90;
            {var subQ0=sQuery(id+"F0.wireOp",EDGE,"E352.MirrorCS");Q90=makeQuery(id+"F0.imprint","IMPRINT",FACE,{"disambiguationData":[TD([[makeQuery(id+"F0.imprint","IMPRINT",EDGE,{"derivedFrom":subQ0}),-1.0]])]});}
            var Q91;
            {var subQ1=sQuery(id+"F0.wireOp",EDGE,"E297.filletArc");Q91=makeQuery(id+"F0.imprint","IMPRINT",FACE,{"disambiguationData":[TD([[makeQuery(id+"F0.imprint","IMPRINT",EDGE,{"derivedFrom":subQ1}),1.0]])]});}
            var Q92;
            {var subQ0=sQuery(id+"F0.wireOp",EDGE,"E337.filletArc");Q92=makeQuery(id+"F0.imprint","IMPRINT",FACE,{"disambiguationData":[TD([[makeQuery(id+"F0.imprint","IMPRINT",EDGE,{"derivedFrom":subQ0}),1.0]])]});}
            var Q93;
            {var subQ0=sQuery(id+"F0.wireOp",EDGE,"E281.filletArc");Q93=makeQuery(id+"F0.imprint","IMPRINT",FACE,{"disambiguationData":[TD([[makeQuery(id+"F0.imprint","IMPRINT",EDGE,{"derivedFrom":subQ0}),1.0]])]});}
            var Q94;
            {var subQ0=sQuery(id+"F0.wireOp",EDGE,"E329.filletArc");Q94=makeQuery(id+"F0.imprint","IMPRINT",FACE,{"disambiguationData":[TD([[makeQuery(id+"F0.imprint","IMPRINT",EDGE,{"derivedFrom":subQ0}),1.0]])]});}
            var Q95;
            {var subQ1=sQuery(id+"F0.wireOp",EDGE,"E367.MirrorCS");Q95=makeQuery(id+"F0.imprint","IMPRINT",FACE,{"disambiguationData":[TD([[makeQuery(id+"F0.imprint","IMPRINT",EDGE,{"derivedFrom":subQ1}),-1.0]])]});}
            var Q96;
            Q96=makeQuery(id+"F0.imprint","IMPRINT",FACE,{"disambiguationData":[TD([[makeQuery(id+"F0.imprint","IMPRINT",EDGE,{"derivedFrom":sQuery(id+"F0.wireOp",EDGE,"E300")}),-1.0]])]});
            var Q97;
            Q97=makeQuery(id+"F0.imprint","IMPRINT",FACE,{"disambiguationData":[TD([[makeQuery(id+"F0.imprint","IMPRINT",EDGE,{"derivedFrom":sQuery(id+"F0.wireOp",EDGE,"E436")}),-1.0]])]});
            var Q98;
            {var subQ0=sQuery(id+"F0.wireOp",EDGE,"E313.filletArc");Q98=makeQuery(id+"F0.imprint","IMPRINT",FACE,{"disambiguationData":[TD([[makeQuery(id+"F0.imprint","IMPRINT",EDGE,{"derivedFrom":subQ0}),1.0]])]});}
            var Q99;
            Q99=makeQuery(id+"F0.imprint","IMPRINT",FACE,{"disambiguationData":[TD([[makeQuery(id+"F0.imprint","IMPRINT",EDGE,{"derivedFrom":sQuery(id+"F0.wireOp",EDGE,"E268")}),-1.0]])]});
            var Q100;
            {var subQ1=sQuery(id+"F0.wireOp",EDGE,"E355.MirrorCS");Q100=makeQuery(id+"F0.imprint","IMPRINT",FACE,{"disambiguationData":[TD([[makeQuery(id+"F0.imprint","IMPRINT",EDGE,{"derivedFrom":subQ1}),-1.0]])]});}
            var Q101;
            Q101=makeQuery(id+"F0.imprint","IMPRINT",FACE,{"disambiguationData":[TD([[makeQuery(id+"F0.imprint","IMPRINT",EDGE,{"derivedFrom":sQuery(id+"F0.wireOp",EDGE,"E369.MirrorCS")}),-1.0]])]});
            var Q102;
            {var subQ0=sQuery(id+"F0.wireOp",EDGE,"E388.MirrorCS");Q102=makeQuery(id+"F0.imprint","IMPRINT",FACE,{"disambiguationData":[TD([[makeQuery(id+"F0.imprint","IMPRINT",EDGE,{"derivedFrom":subQ0}),-1.0]])]});}
            var Q103;
            {var subQ0=sQuery(id+"F0.wireOp",EDGE,"E345.filletArc");Q103=makeQuery(id+"F0.imprint","IMPRINT",FACE,{"disambiguationData":[TD([[makeQuery(id+"F0.imprint","IMPRINT",EDGE,{"derivedFrom":subQ0}),1.0]])]});}
            var Q104;
            {var subQ0=sQuery(id+"F0.wireOp",EDGE,"E290");Q104=makeQuery(id+"F0.imprint","IMPRINT",FACE,{"disambiguationData":[TD([[makeQuery(id+"F0.imprint","IMPRINT",EDGE,{"derivedFrom":subQ0}),1.0]])]});}
            var Q105;
            {var subQ1=sQuery(id+"F0.wireOp",EDGE,"E356.MirrorCS");Q105=makeQuery(id+"F0.imprint","IMPRINT",FACE,{"disambiguationData":[TD([[makeQuery(id+"F0.imprint","IMPRINT",EDGE,{"derivedFrom":subQ1}),-1.0]])]});}
            var Q106;
            {var subQ0=sQuery(id+"F0.wireOp",EDGE,"E305.filletArc");Q106=makeQuery(id+"F0.imprint","IMPRINT",FACE,{"disambiguationData":[TD([[makeQuery(id+"F0.imprint","IMPRINT",EDGE,{"derivedFrom":subQ0}),1.0]])]});}
            var Q107;
            {var subQ0=sQuery(id+"F0.wireOp",EDGE,"E441.filletArc");Q107=makeQuery(id+"F0.imprint","IMPRINT",FACE,{"disambiguationData":[TD([[makeQuery(id+"F0.imprint","IMPRINT",EDGE,{"derivedFrom":subQ0}),1.0]])]});}
            var Q108;
            {var subQ5=sQuery(id+"F0.wireOp",EDGE,"E274");Q108=makeQuery(id+"F0.imprint","IMPRINT",FACE,{"disambiguationData":[TD([[makeQuery(id+"F0.imprint","IMPRINT",EDGE,{"derivedFrom":subQ5}),1.0]])]});}
            var Q109;
            {var subQ0=sQuery(id+"F0.wireOp",EDGE,"E321.filletArc");Q109=makeQuery(id+"F0.imprint","IMPRINT",FACE,{"disambiguationData":[TD([[makeQuery(id+"F0.imprint","IMPRINT",EDGE,{"derivedFrom":subQ0}),1.0]])]});}
            var Q110;
            {var subQ5=sQuery(id+"F0.wireOp",EDGE,"E450");Q110=makeQuery(id+"F0.imprint","IMPRINT",FACE,{"disambiguationData":[TD([[makeQuery(id+"F0.imprint","IMPRINT",EDGE,{"derivedFrom":subQ5}),1.0]])]});}
            var Q111;
            {var subQ5=sQuery(id+"F0.wireOp",EDGE,"E425.MirrorCS");Q111=makeQuery(id+"F0.imprint","IMPRINT",FACE,{"disambiguationData":[TD([[makeQuery(id+"F0.imprint","IMPRINT",EDGE,{"derivedFrom":subQ5}),-1.0]])]});}
            var Q112;
            {var subQ5=sQuery(id+"F0.wireOp",EDGE,"E392.MirrorCS");Q112=makeQuery(id+"F0.imprint","IMPRINT",FACE,{"disambiguationData":[TD([[makeQuery(id+"F0.imprint","IMPRINT",EDGE,{"derivedFrom":subQ5}),-1.0]])]});}
            var Q113;
            {var subQ1=sQuery(id+"F0.wireOp",EDGE,"E357.MirrorCS");Q113=makeQuery(id+"F0.imprint","IMPRINT",FACE,{"disambiguationData":[TD([[makeQuery(id+"F0.imprint","IMPRINT",EDGE,{"derivedFrom":subQ1}),-1.0]])]});}
            var Q114;
            {var subQ5=sQuery(id+"F0.wireOp",EDGE,"E393.MirrorCS");Q114=makeQuery(id+"F0.imprint","IMPRINT",FACE,{"disambiguationData":[TD([[makeQuery(id+"F0.imprint","IMPRINT",EDGE,{"derivedFrom":subQ5}),-1.0]])]});}
            var Q115;
            {var subQ4=sQuery(id+"F0.wireOp",EDGE,"E348.MirrorCS");Q115=makeQuery(id+"F0.imprint","IMPRINT",FACE,{"disambiguationData":[TD([[makeQuery(id+"F0.imprint","IMPRINT",EDGE,{"derivedFrom":subQ4}),-1.0]])]});}
            var Q116;
            {var subQ1=sQuery(id+"F0.wireOp",EDGE,"E387.MirrorCS");Q116=makeQuery(id+"F0.imprint","IMPRINT",FACE,{"disambiguationData":[TD([[makeQuery(id+"F0.imprint","IMPRINT",EDGE,{"derivedFrom":subQ1}),-1.0]])]});}
            var Q117;
            {var subQ1=sQuery(id+"F0.wireOp",EDGE,"E358.MirrorCS");Q117=makeQuery(id+"F0.imprint","IMPRINT",FACE,{"disambiguationData":[TD([[makeQuery(id+"F0.imprint","IMPRINT",EDGE,{"derivedFrom":subQ1}),-1.0]])]});}
            var Q118;
            {var subQ1=sQuery(id+"F0.wireOp",EDGE,"E351.MirrorCS");Q118=makeQuery(id+"F0.imprint","IMPRINT",FACE,{"disambiguationData":[TD([[makeQuery(id+"F0.imprint","IMPRINT",EDGE,{"derivedFrom":subQ1}),-1.0]])]});}
            extrude(context, id + "F1", {"entities" : qUnion([Q0, Q1, Q2, Q3, Q4, Q5, Q6, Q7, Q8, Q9, Q10, Q11, Q12, Q13, Q14, Q15, Q16, Q17, Q18, Q19, Q20, Q21, Q22, Q23, Q24, Q25, Q26, Q27, Q28, Q29, Q30, Q31, Q32, Q33, Q34, Q35, Q36, Q37, Q38, Q39, Q40, Q41, Q42, Q43, Q44, Q45, Q46, Q47, Q48, Q49, Q50, Q51, Q52, Q53, Q54, Q55, Q56, Q57, Q58, Q59, Q60, Q61, Q62, Q63, Q64, Q65, Q66, Q67, Q68, Q69, Q70, Q71, Q72, Q73, Q74, Q75, Q76, Q77, Q78, Q79, Q80, Q81, Q82, Q83, Q84, Q85, Q86, Q87, Q88, Q89, Q90, Q91, Q92, Q93, Q94, Q95, Q96, Q97, Q98, Q99, Q100, Q101, Q102, Q103, Q104, Q105, Q106, Q107, Q108, Q109, Q110, Q111, Q112, Q113, Q114, Q115, Q116, Q117, Q118]), "depth" : 12.7 * mm});
        }
        {
            var Q0;
            Q0 = qSketchRegion(id + "F0", true);
            extrude(context, id + "F2", {"entities" : qUnion([Q0]), "depth" : 25.4 * mm});
        }
    });
